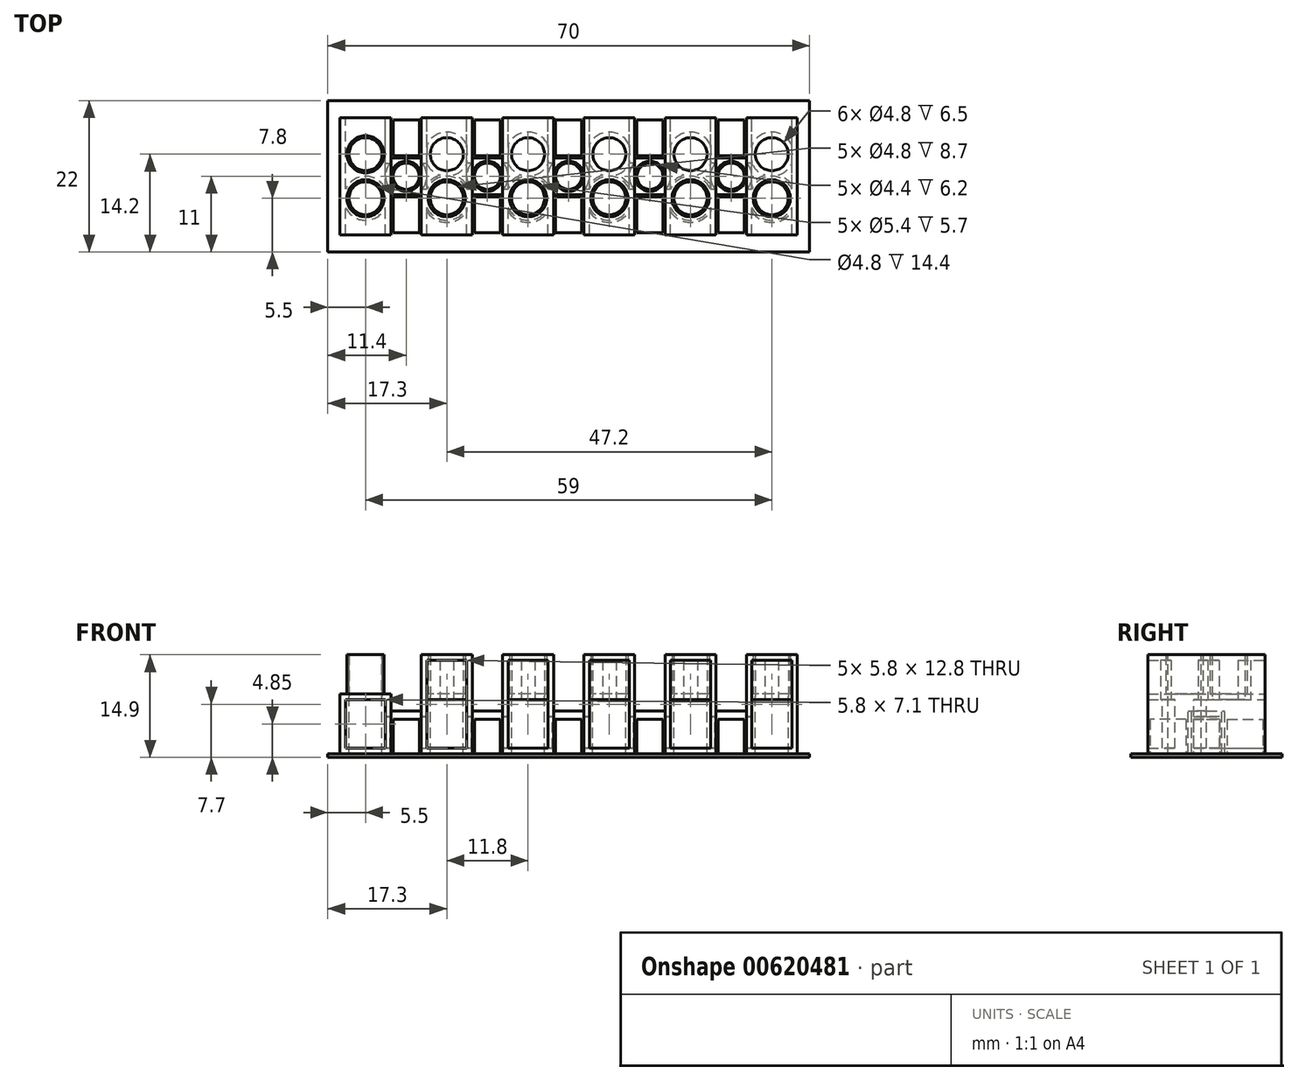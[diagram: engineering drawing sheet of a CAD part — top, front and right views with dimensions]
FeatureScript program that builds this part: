
annotation { "Feature Type Name" : "Feature", "Feature Type Description" : "" }
export const myFeature = defineFeature(function(context is Context, id is Id, definition is map)
    precondition{}
    {
        {
            var Q0;
            Q0=qCreatedBy(makeId("Top.planeOp"),FACE);
            var sketch = newSketch(context, id + "F0", { "sketchPlane" : qUnion([Q0])});
            skLineSegment(sketch, "E0.bottom", {"start": v(-25.8, -8.5) * mm, "end": v(-33.2, -8.5) * mm});
            skLineSegment(sketch, "E0.top", {"start": v(-25.8, 8.5) * mm, "end": v(-33.2, 8.5) * mm});
            skLineSegment(sketch, "E0.left", {"start": v(-25.8, -8.5) * mm, "end": v(-25.8, 8.5) * mm});
            skLineSegment(sketch, "E0.right", {"start": v(-33.2, -8.5) * mm, "end": v(-33.2, 8.5) * mm});
            skLineSegment(sketch, "E1.bottom", {"start": v(-14, -8.5) * mm, "end": v(-21.4, -8.5) * mm});
            skLineSegment(sketch, "E1.top", {"start": v(-14, 8.5) * mm, "end": v(-21.4, 8.5) * mm});
            skLineSegment(sketch, "E1.left", {"start": v(-14, -8.5) * mm, "end": v(-14, 8.5) * mm});
            skLineSegment(sketch, "E1.right", {"start": v(-21.4, -8.5) * mm, "end": v(-21.4, 8.5) * mm});
            skLineSegment(sketch, "E2.bottom", {"start": v(-2.2, -8.5) * mm, "end": v(-9.6, -8.5) * mm});
            skLineSegment(sketch, "E2.top", {"start": v(-2.2, 8.5) * mm, "end": v(-9.6, 8.5) * mm});
            skLineSegment(sketch, "E2.left", {"start": v(-2.2, -8.5) * mm, "end": v(-2.2, 8.5) * mm});
            skLineSegment(sketch, "E2.right", {"start": v(-9.6, -8.5) * mm, "end": v(-9.6, 8.5) * mm});
            skLineSegment(sketch, "E3.bottom", {"start": v(9.6, -8.5) * mm, "end": v(2.2, -8.5) * mm});
            skLineSegment(sketch, "E3.top", {"start": v(9.6, 8.5) * mm, "end": v(2.2, 8.5) * mm});
            skLineSegment(sketch, "E3.left", {"start": v(9.6, -8.5) * mm, "end": v(9.6, 8.5) * mm});
            skLineSegment(sketch, "E3.right", {"start": v(2.2, -8.5) * mm, "end": v(2.2, 8.5) * mm});
            skLineSegment(sketch, "E4.bottom", {"start": v(21.4, -8.5) * mm, "end": v(14, -8.5) * mm});
            skLineSegment(sketch, "E4.top", {"start": v(21.4, 8.5) * mm, "end": v(14, 8.5) * mm});
            skLineSegment(sketch, "E4.left", {"start": v(21.4, -8.5) * mm, "end": v(21.4, 8.5) * mm});
            skLineSegment(sketch, "E4.right", {"start": v(14, -8.5) * mm, "end": v(14, 8.5) * mm});
            skLineSegment(sketch, "E5.bottom", {"start": v(33.2, -8.5) * mm, "end": v(25.8, -8.5) * mm});
            skLineSegment(sketch, "E5.top", {"start": v(33.2, 8.5) * mm, "end": v(25.8, 8.5) * mm});
            skLineSegment(sketch, "E5.left", {"start": v(33.2, -8.5) * mm, "end": v(33.2, 8.5) * mm});
            skLineSegment(sketch, "E5.right", {"start": v(25.8, -8.5) * mm, "end": v(25.8, 8.5) * mm});
            skCircle(sketch, "E6", {"center": v(-29.5, 3.2) * mm, "radius": 2.7 * mm});
            skCircle(sketch, "E7", {"center": v(-29.5, -3.2) * mm, "radius": 2.7 * mm});
            skCircle(sketch, "E8", {"center": v(-17.7, 3.2) * mm, "radius": 2.7 * mm});
            skCircle(sketch, "E9", {"center": v(-5.9, 3.2) * mm, "radius": 2.7 * mm});
            skCircle(sketch, "E10", {"center": v(5.9, 3.2) * mm, "radius": 2.7 * mm});
            skCircle(sketch, "E11", {"center": v(17.7, 3.2) * mm, "radius": 2.7 * mm});
            skCircle(sketch, "E12", {"center": v(29.5, 3.2) * mm, "radius": 2.7 * mm});
            skCircle(sketch, "E13.MirrorC", {"center": v(-17.7, -3.2) * mm, "radius": 2.7 * mm});
            skCircle(sketch, "E14.MirrorC", {"center": v(-5.9, -3.2) * mm, "radius": 2.7 * mm});
            skCircle(sketch, "E15.MirrorC", {"center": v(5.9, -3.2) * mm, "radius": 2.7 * mm});
            skCircle(sketch, "E16.MirrorC", {"center": v(17.7, -3.2) * mm, "radius": 2.7 * mm});
            skCircle(sketch, "E17.MirrorC", {"center": v(29.5, -3.2) * mm, "radius": 2.7 * mm});
            skCircle(sketch, "E18.0", {"center": v(-29.5, 3.2) * mm, "radius": 2.4 * mm});
            skCircle(sketch, "E19.0", {"center": v(-17.7, 3.2) * mm, "radius": 2.4 * mm});
            skCircle(sketch, "E20.0", {"center": v(-5.9, 3.2) * mm, "radius": 2.4 * mm});
            skCircle(sketch, "E21.0", {"center": v(5.9, 3.2) * mm, "radius": 2.4 * mm});
            skCircle(sketch, "E22.0", {"center": v(17.7, 3.2) * mm, "radius": 2.4 * mm});
            skCircle(sketch, "E23.0", {"center": v(29.5, 3.2) * mm, "radius": 2.4 * mm});
            skCircle(sketch, "E24.MirrorC", {"center": v(-29.5, -3.2) * mm, "radius": 2.4 * mm});
            skCircle(sketch, "E25.MirrorC", {"center": v(-17.7, -3.2) * mm, "radius": 2.4 * mm});
            skCircle(sketch, "E26.MirrorC", {"center": v(-5.9, -3.2) * mm, "radius": 2.4 * mm});
            skCircle(sketch, "E27.MirrorC", {"center": v(5.9, -3.2) * mm, "radius": 2.4 * mm});
            skCircle(sketch, "E28.MirrorC", {"center": v(17.7, -3.2) * mm, "radius": 2.4 * mm});
            skCircle(sketch, "E29.MirrorC", {"center": v(29.5, -3.2) * mm, "radius": 2.4 * mm});
            skCircle(sketch, "E30", {"center": v(0, 0) * mm, "radius": 0.25 * mm, "construction": true});
            skLineSegment(sketch, "E31", {"start": v(0, 0) * mm, "end": v(0, -17.47) * mm, "construction": true});
            skLineSegment(sketch, "E32", {"start": v(-29.5, 8.5) * mm, "end": v(-29.5, -8.5) * mm, "construction": true});
            skLineSegment(sketch, "E33", {"start": v(-17.7, 8.5) * mm, "end": v(-17.7, -8.5) * mm, "construction": true});
            skLineSegment(sketch, "E34", {"start": v(-5.9, 8.5) * mm, "end": v(-5.9, -8.5) * mm, "construction": true});
            skLineSegment(sketch, "E35", {"start": v(5.9, 8.5) * mm, "end": v(5.9, -8.5) * mm, "construction": true});
            skLineSegment(sketch, "E36", {"start": v(17.7, 8.5) * mm, "end": v(17.7, -8.5) * mm, "construction": true});
            skLineSegment(sketch, "E37", {"start": v(29.5, 8.5) * mm, "end": v(29.5, -8.5) * mm, "construction": true});
            skLineSegment(sketch, "E38", {"start": v(-33.2, 0) * mm, "end": v(33.2, 0) * mm, "construction": true});
            skLineSegment(sketch, "E39", {"start": v(-25.8, 2.68) * mm, "end": v(-21.4, 2.68) * mm});
            skLineSegment(sketch, "E40", {"start": v(-25.8, -2.68) * mm, "end": v(-21.4, -2.68) * mm});
            skLineSegment(sketch, "E41", {"start": v(-14, -2.68) * mm, "end": v(-9.6, -2.68) * mm});
            skLineSegment(sketch, "E42", {"start": v(-2.2, -2.68) * mm, "end": v(2.2, -2.68) * mm});
            skLineSegment(sketch, "E43", {"start": v(9.6, -2.68) * mm, "end": v(14, -2.68) * mm});
            skLineSegment(sketch, "E44", {"start": v(21.4, -2.68) * mm, "end": v(25.8, -2.68) * mm});
            skLineSegment(sketch, "E45", {"start": v(25.8, 2.68) * mm, "end": v(21.4, 2.68) * mm});
            skLineSegment(sketch, "E46", {"start": v(14, 2.68) * mm, "end": v(9.6, 2.68) * mm});
            skLineSegment(sketch, "E47", {"start": v(2.2, 2.68) * mm, "end": v(-2.2, 2.68) * mm});
            skLineSegment(sketch, "E48", {"start": v(-9.6, 2.68) * mm, "end": v(-14, 2.68) * mm});
            skLineSegment(sketch, "E49", {"start": v(-25.8, 2.68) * mm, "end": v(-21.4, -2.68) * mm, "construction": true});
            skLineSegment(sketch, "E50", {"start": v(-14, 2.68) * mm, "end": v(-9.6, -2.68) * mm, "construction": true});
            skLineSegment(sketch, "E51", {"start": v(-2.2, 2.68) * mm, "end": v(2.2, -2.68) * mm, "construction": true});
            skLineSegment(sketch, "E52", {"start": v(9.6, 2.68) * mm, "end": v(14, -2.68) * mm, "construction": true});
            skLineSegment(sketch, "E53", {"start": v(21.4, 2.68) * mm, "end": v(25.8, -2.68) * mm, "construction": true});
            skCircle(sketch, "E54", {"center": v(-23.6, 0) * mm, "radius": 2.2 * mm});
            skCircle(sketch, "E55", {"center": v(-11.8, 0) * mm, "radius": 2.2 * mm});
            skCircle(sketch, "E56", {"center": v(0, 0) * mm, "radius": 2.2 * mm});
            skCircle(sketch, "E57", {"center": v(11.8, 0) * mm, "radius": 2.2 * mm});
            skCircle(sketch, "E58", {"center": v(23.6, 0) * mm, "radius": 2.2 * mm});
            skSolve(sketch);
        }
        {
            var Q0;
            {var subQ3=sQuery(id+"F0.wireOp",EDGE,"E0.bottom");Q0=makeQuery(id+"F0.imprint","IMPRINT",FACE,{"disambiguationData":[TD([[makeQuery(id+"F0.imprint","IMPRINT",EDGE,{"derivedFrom":subQ3}),-1.0]])]});}
            var Q1;
            {var subQ5=sQuery(id+"F0.wireOp",EDGE,"E1.bottom");Q1=makeQuery(id+"F0.imprint","IMPRINT",FACE,{"disambiguationData":[TD([[makeQuery(id+"F0.imprint","IMPRINT",EDGE,{"derivedFrom":subQ5}),-1.0]])]});}
            var Q2;
            {var subQ5=sQuery(id+"F0.wireOp",EDGE,"E2.bottom");Q2=makeQuery(id+"F0.imprint","IMPRINT",FACE,{"disambiguationData":[TD([[makeQuery(id+"F0.imprint","IMPRINT",EDGE,{"derivedFrom":subQ5}),-1.0]])]});}
            var Q3;
            {var subQ5=sQuery(id+"F0.wireOp",EDGE,"E3.bottom");Q3=makeQuery(id+"F0.imprint","IMPRINT",FACE,{"disambiguationData":[TD([[makeQuery(id+"F0.imprint","IMPRINT",EDGE,{"derivedFrom":subQ5}),-1.0]])]});}
            var Q4;
            {var subQ5=sQuery(id+"F0.wireOp",EDGE,"E4.bottom");Q4=makeQuery(id+"F0.imprint","IMPRINT",FACE,{"disambiguationData":[TD([[makeQuery(id+"F0.imprint","IMPRINT",EDGE,{"derivedFrom":subQ5}),-1.0]])]});}
            var Q5;
            {var subQ1=sQuery(id+"F0.wireOp",EDGE,"E5.bottom");Q5=makeQuery(id+"F0.imprint","IMPRINT",FACE,{"disambiguationData":[TD([[makeQuery(id+"F0.imprint","IMPRINT",EDGE,{"derivedFrom":subQ1}),-1.0]])]});}
            var Q6;
            {var subQ0=sQuery(id+"F0.wireOp",EDGE,"d3VJdfNO-Fk8P-fh5y-onYD-prEol703JRMM");Q6=makeQuery(id+"F0.imprint","IMPRINT",FACE,{"disambiguationData":[TD([[makeQuery(id+"F0.imprint","IMPRINT",EDGE,{"derivedFrom":subQ0}),1.0]])]});}
            var Q7;
            {var subQ0=sQuery(id+"F0.wireOp",EDGE,"IIVYpRpw-wNBd-OXcb-W0MZ-mRHXIPyjJA5R");Q7=makeQuery(id+"F0.imprint","IMPRINT",FACE,{"disambiguationData":[TD([[makeQuery(id+"F0.imprint","IMPRINT",EDGE,{"derivedFrom":subQ0}),1.0]])]});}
            var Q8;
            {var subQ0=sQuery(id+"F0.wireOp",EDGE,"wgGCBpVZ-QxlM-H5Bi-xMEc-6BhFhbDtORX5");Q8=makeQuery(id+"F0.imprint","IMPRINT",FACE,{"disambiguationData":[TD([[makeQuery(id+"F0.imprint","IMPRINT",EDGE,{"derivedFrom":subQ0}),-1.0]])]});}
            var Q9;
            {var subQ0=sQuery(id+"F0.wireOp",EDGE,"S4L2WrHO-g6c6-6cLC-dkaz-DY6cZUDI1iXS");Q9=makeQuery(id+"F0.imprint","IMPRINT",FACE,{"disambiguationData":[TD([[makeQuery(id+"F0.imprint","IMPRINT",EDGE,{"derivedFrom":subQ0}),-1.0]])]});}
            var Q10;
            {var subQ0=sQuery(id+"F0.wireOp",EDGE,"iaEsDPjX-zqyW-dyph-9nWc-KghkqS62flJh");Q10=makeQuery(id+"F0.imprint","IMPRINT",FACE,{"disambiguationData":[TD([[makeQuery(id+"F0.imprint","IMPRINT",EDGE,{"derivedFrom":subQ0}),-1.0]])]});}
            var Q11;
            {var subQ0=sQuery(id+"F0.wireOp",EDGE,"gJlDzY57-16t4-Vf8D-4nsT-QQv6MURsNHDC");Q11=makeQuery(id+"F0.imprint","IMPRINT",FACE,{"disambiguationData":[TD([[makeQuery(id+"F0.imprint","IMPRINT",EDGE,{"derivedFrom":subQ0}),1.0]])]});}
            var Q12;
            {var subQ0=sQuery(id+"F0.wireOp",EDGE,"vcY6GDkU-c4bm-z2yD-HaH5-KhH9jC7oKOPS");Q12=makeQuery(id+"F0.imprint","IMPRINT",FACE,{"disambiguationData":[TD([[makeQuery(id+"F0.imprint","IMPRINT",EDGE,{"derivedFrom":subQ0}),1.0]])]});}
            var Q13;
            {var subQ0=sQuery(id+"F0.wireOp",EDGE,"J0IPBTmc-wLEG-zjEr-TODg-CiZrFgkn9riR");Q13=makeQuery(id+"F0.imprint","IMPRINT",FACE,{"disambiguationData":[TD([[makeQuery(id+"F0.imprint","IMPRINT",EDGE,{"derivedFrom":subQ0}),-1.0]])]});}
            var Q14;
            {var subQ0=sQuery(id+"F0.wireOp",EDGE,"VlebEy6t-9yxg-sLxx-iXkv-Cso8guSqJYIt");Q14=makeQuery(id+"F0.imprint","IMPRINT",FACE,{"disambiguationData":[TD([[makeQuery(id+"F0.imprint","IMPRINT",EDGE,{"derivedFrom":subQ0}),-1.0]])]});}
            var Q15;
            {var subQ0=sQuery(id+"F0.wireOp",EDGE,"8PrGnW9D-uxJ0-gMwz-QmAr-Uvm73S1oeha5");Q15=makeQuery(id+"F0.imprint","IMPRINT",FACE,{"disambiguationData":[TD([[makeQuery(id+"F0.imprint","IMPRINT",EDGE,{"derivedFrom":subQ0}),1.0]])]});}
            var Q16;
            Q16=makeQuery(id+"F0.imprint","IMPRINT",FACE,{"disambiguationData":[TD([[makeQuery(id+"F0.imprint","IMPRINT",EDGE,{"derivedFrom":sQuery(id+"F0.wireOp",EDGE,"E6")}),1.0]])]});
            var Q17;
            Q17=makeQuery(id+"F0.imprint","IMPRINT",FACE,{"disambiguationData":[TD([[makeQuery(id+"F0.imprint","IMPRINT",EDGE,{"derivedFrom":sQuery(id+"F0.wireOp",EDGE,"E7")}),1.0]])]});
            var Q18;
            Q18=makeQuery(id+"F0.imprint","IMPRINT",FACE,{"disambiguationData":[TD([[makeQuery(id+"F0.imprint","IMPRINT",EDGE,{"derivedFrom":sQuery(id+"F0.wireOp",EDGE,"E13.MirrorC")}),-1.0]])]});
            var Q19;
            Q19=makeQuery(id+"F0.imprint","IMPRINT",FACE,{"disambiguationData":[TD([[makeQuery(id+"F0.imprint","IMPRINT",EDGE,{"derivedFrom":sQuery(id+"F0.wireOp",EDGE,"E8")}),1.0]])]});
            var Q20;
            Q20=makeQuery(id+"F0.imprint","IMPRINT",FACE,{"disambiguationData":[TD([[makeQuery(id+"F0.imprint","IMPRINT",EDGE,{"derivedFrom":sQuery(id+"F0.wireOp",EDGE,"E14.MirrorC")}),-1.0]])]});
            var Q21;
            Q21=makeQuery(id+"F0.imprint","IMPRINT",FACE,{"disambiguationData":[TD([[makeQuery(id+"F0.imprint","IMPRINT",EDGE,{"derivedFrom":sQuery(id+"F0.wireOp",EDGE,"E15.MirrorC")}),-1.0]])]});
            var Q22;
            Q22=makeQuery(id+"F0.imprint","IMPRINT",FACE,{"disambiguationData":[TD([[makeQuery(id+"F0.imprint","IMPRINT",EDGE,{"derivedFrom":sQuery(id+"F0.wireOp",EDGE,"E10")}),1.0]])]});
            var Q23;
            Q23=makeQuery(id+"F0.imprint","IMPRINT",FACE,{"disambiguationData":[TD([[makeQuery(id+"F0.imprint","IMPRINT",EDGE,{"derivedFrom":sQuery(id+"F0.wireOp",EDGE,"E16.MirrorC")}),-1.0]])]});
            var Q24;
            Q24=makeQuery(id+"F0.imprint","IMPRINT",FACE,{"disambiguationData":[TD([[makeQuery(id+"F0.imprint","IMPRINT",EDGE,{"derivedFrom":sQuery(id+"F0.wireOp",EDGE,"E11")}),1.0]])]});
            var Q25;
            Q25=makeQuery(id+"F0.imprint","IMPRINT",FACE,{"disambiguationData":[TD([[makeQuery(id+"F0.imprint","IMPRINT",EDGE,{"derivedFrom":sQuery(id+"F0.wireOp",EDGE,"E17.MirrorC")}),-1.0]])]});
            var Q26;
            Q26=makeQuery(id+"F0.imprint","IMPRINT",FACE,{"disambiguationData":[TD([[makeQuery(id+"F0.imprint","IMPRINT",EDGE,{"derivedFrom":sQuery(id+"F0.wireOp",EDGE,"E12")}),1.0]])]});
            var Q27;
            Q27=makeQuery(id+"F0.imprint","IMPRINT",FACE,{"disambiguationData":[TD([[makeQuery(id+"F0.imprint","IMPRINT",EDGE,{"derivedFrom":sQuery(id+"F0.wireOp",EDGE,"E9")}),1.0]])]});
            var Q28;
            Q28=makeQuery(id+"F0.imprint","IMPRINT",FACE,{"disambiguationData":[TD([[makeQuery(id+"F0.imprint","IMPRINT",EDGE,{"derivedFrom":sQuery(id+"F0.wireOp",EDGE,"E18.0")}),1.0]])]});
            var Q29;
            Q29=makeQuery(id+"F0.imprint","IMPRINT",FACE,{"disambiguationData":[TD([[makeQuery(id+"F0.imprint","IMPRINT",EDGE,{"derivedFrom":sQuery(id+"F0.wireOp",EDGE,"E24.MirrorC")}),-1.0]])]});
            var Q30;
            Q30=makeQuery(id+"F0.imprint","IMPRINT",FACE,{"disambiguationData":[TD([[makeQuery(id+"F0.imprint","IMPRINT",EDGE,{"derivedFrom":sQuery(id+"F0.wireOp",EDGE,"E19.0")}),1.0]])]});
            var Q31;
            Q31=makeQuery(id+"F0.imprint","IMPRINT",FACE,{"disambiguationData":[TD([[makeQuery(id+"F0.imprint","IMPRINT",EDGE,{"derivedFrom":sQuery(id+"F0.wireOp",EDGE,"E25.MirrorC")}),-1.0]])]});
            var Q32;
            Q32=makeQuery(id+"F0.imprint","IMPRINT",FACE,{"disambiguationData":[TD([[makeQuery(id+"F0.imprint","IMPRINT",EDGE,{"derivedFrom":sQuery(id+"F0.wireOp",EDGE,"E20.0")}),1.0]])]});
            var Q33;
            Q33=makeQuery(id+"F0.imprint","IMPRINT",FACE,{"disambiguationData":[TD([[makeQuery(id+"F0.imprint","IMPRINT",EDGE,{"derivedFrom":sQuery(id+"F0.wireOp",EDGE,"E26.MirrorC")}),-1.0]])]});
            var Q34;
            Q34=makeQuery(id+"F0.imprint","IMPRINT",FACE,{"disambiguationData":[TD([[makeQuery(id+"F0.imprint","IMPRINT",EDGE,{"derivedFrom":sQuery(id+"F0.wireOp",EDGE,"E21.0")}),1.0]])]});
            var Q35;
            Q35=makeQuery(id+"F0.imprint","IMPRINT",FACE,{"disambiguationData":[TD([[makeQuery(id+"F0.imprint","IMPRINT",EDGE,{"derivedFrom":sQuery(id+"F0.wireOp",EDGE,"E27.MirrorC")}),-1.0]])]});
            var Q36;
            Q36=makeQuery(id+"F0.imprint","IMPRINT",FACE,{"disambiguationData":[TD([[makeQuery(id+"F0.imprint","IMPRINT",EDGE,{"derivedFrom":sQuery(id+"F0.wireOp",EDGE,"E22.0")}),1.0]])]});
            var Q37;
            Q37=makeQuery(id+"F0.imprint","IMPRINT",FACE,{"disambiguationData":[TD([[makeQuery(id+"F0.imprint","IMPRINT",EDGE,{"derivedFrom":sQuery(id+"F0.wireOp",EDGE,"E28.MirrorC")}),-1.0]])]});
            var Q38;
            Q38=makeQuery(id+"F0.imprint","IMPRINT",FACE,{"disambiguationData":[TD([[makeQuery(id+"F0.imprint","IMPRINT",EDGE,{"derivedFrom":sQuery(id+"F0.wireOp",EDGE,"E29.MirrorC")}),-1.0]])]});
            var Q39;
            Q39=makeQuery(id+"F0.imprint","IMPRINT",FACE,{"disambiguationData":[TD([[makeQuery(id+"F0.imprint","IMPRINT",EDGE,{"derivedFrom":sQuery(id+"F0.wireOp",EDGE,"E23.0")}),1.0]])]});
            var Q40;
            {var subQ0=sQuery(id+"F0.wireOp",EDGE,"E40");Q40=makeQuery(id+"F0.imprint","IMPRINT",FACE,{"disambiguationData":[TD([[makeQuery(id+"F0.imprint","IMPRINT",EDGE,{"derivedFrom":subQ0}),1.0]])]});}
            var Q41;
            {var subQ0=sQuery(id+"F0.wireOp",EDGE,"E39");Q41=makeQuery(id+"F0.imprint","IMPRINT",FACE,{"disambiguationData":[TD([[makeQuery(id+"F0.imprint","IMPRINT",EDGE,{"derivedFrom":subQ0}),-1.0]])]});}
            var Q42;
            {var subQ0=sQuery(id+"F0.wireOp",EDGE,"E48");Q42=makeQuery(id+"F0.imprint","IMPRINT",FACE,{"disambiguationData":[TD([[makeQuery(id+"F0.imprint","IMPRINT",EDGE,{"derivedFrom":subQ0}),1.0]])]});}
            var Q43;
            {var subQ0=sQuery(id+"F0.wireOp",EDGE,"E41");Q43=makeQuery(id+"F0.imprint","IMPRINT",FACE,{"disambiguationData":[TD([[makeQuery(id+"F0.imprint","IMPRINT",EDGE,{"derivedFrom":subQ0}),1.0]])]});}
            var Q44;
            {var subQ0=sQuery(id+"F0.wireOp",EDGE,"E47");Q44=makeQuery(id+"F0.imprint","IMPRINT",FACE,{"disambiguationData":[TD([[makeQuery(id+"F0.imprint","IMPRINT",EDGE,{"derivedFrom":subQ0}),1.0]])]});}
            var Q45;
            {var subQ0=sQuery(id+"F0.wireOp",EDGE,"E42");Q45=makeQuery(id+"F0.imprint","IMPRINT",FACE,{"disambiguationData":[TD([[makeQuery(id+"F0.imprint","IMPRINT",EDGE,{"derivedFrom":subQ0}),1.0]])]});}
            var Q46;
            {var subQ0=sQuery(id+"F0.wireOp",EDGE,"E46");Q46=makeQuery(id+"F0.imprint","IMPRINT",FACE,{"disambiguationData":[TD([[makeQuery(id+"F0.imprint","IMPRINT",EDGE,{"derivedFrom":subQ0}),1.0]])]});}
            var Q47;
            {var subQ0=sQuery(id+"F0.wireOp",EDGE,"E43");Q47=makeQuery(id+"F0.imprint","IMPRINT",FACE,{"disambiguationData":[TD([[makeQuery(id+"F0.imprint","IMPRINT",EDGE,{"derivedFrom":subQ0}),1.0]])]});}
            var Q48;
            {var subQ0=sQuery(id+"F0.wireOp",EDGE,"E45");Q48=makeQuery(id+"F0.imprint","IMPRINT",FACE,{"disambiguationData":[TD([[makeQuery(id+"F0.imprint","IMPRINT",EDGE,{"derivedFrom":subQ0}),1.0]])]});}
            var Q49;
            {var subQ0=sQuery(id+"F0.wireOp",EDGE,"E44");Q49=makeQuery(id+"F0.imprint","IMPRINT",FACE,{"disambiguationData":[TD([[makeQuery(id+"F0.imprint","IMPRINT",EDGE,{"derivedFrom":subQ0}),1.0]])]});}
            extrude(context, id + "F1", {"entities" : qUnion([Q0, Q1, Q2, Q3, Q4, Q5, Q6, Q7, Q8, Q9, Q10, Q11, Q12, Q13, Q14, Q15, Q16, Q17, Q18, Q19, Q20, Q21, Q22, Q23, Q24, Q25, Q26, Q27, Q28, Q29, Q30, Q31, Q32, Q33, Q34, Q35, Q36, Q37, Q38, Q39, Q40, Q41, Q42, Q43, Q44, Q45, Q46, Q47, Q48, Q49]), "oppositeDirection" : true, "depth" : 8.7 * mm, "offsetDistance" : 25 * mm});
        }
        {
            var Q0;
            Q0=makeQuery(id+"F0.imprint","IMPRINT",FACE,{"disambiguationData":[TD([[makeQuery(id+"F0.imprint","IMPRINT",EDGE,{"derivedFrom":sQuery(id+"F0.wireOp",EDGE,"E7")}),1.0]])]});
            var Q1;
            Q1=makeQuery(id+"F0.imprint","IMPRINT",FACE,{"disambiguationData":[TD([[makeQuery(id+"F0.imprint","IMPRINT",EDGE,{"derivedFrom":sQuery(id+"F0.wireOp",EDGE,"E6")}),1.0]])]});
            var Q2;
            Q2=makeQuery(id+"F0.imprint","IMPRINT",FACE,{"disambiguationData":[TD([[makeQuery(id+"F0.imprint","IMPRINT",EDGE,{"derivedFrom":sQuery(id+"F0.wireOp",EDGE,"E8")}),1.0]])]});
            var Q3;
            Q3=makeQuery(id+"F0.imprint","IMPRINT",FACE,{"disambiguationData":[TD([[makeQuery(id+"F0.imprint","IMPRINT",EDGE,{"derivedFrom":sQuery(id+"F0.wireOp",EDGE,"E13.MirrorC")}),-1.0]])]});
            var Q4;
            Q4=makeQuery(id+"F0.imprint","IMPRINT",FACE,{"disambiguationData":[TD([[makeQuery(id+"F0.imprint","IMPRINT",EDGE,{"derivedFrom":sQuery(id+"F0.wireOp",EDGE,"E14.MirrorC")}),-1.0]])]});
            var Q5;
            Q5=makeQuery(id+"F0.imprint","IMPRINT",FACE,{"disambiguationData":[TD([[makeQuery(id+"F0.imprint","IMPRINT",EDGE,{"derivedFrom":sQuery(id+"F0.wireOp",EDGE,"E9")}),1.0]])]});
            var Q6;
            Q6=makeQuery(id+"F0.imprint","IMPRINT",FACE,{"disambiguationData":[TD([[makeQuery(id+"F0.imprint","IMPRINT",EDGE,{"derivedFrom":sQuery(id+"F0.wireOp",EDGE,"E15.MirrorC")}),-1.0]])]});
            var Q7;
            Q7=makeQuery(id+"F0.imprint","IMPRINT",FACE,{"disambiguationData":[TD([[makeQuery(id+"F0.imprint","IMPRINT",EDGE,{"derivedFrom":sQuery(id+"F0.wireOp",EDGE,"E10")}),1.0]])]});
            var Q8;
            Q8=makeQuery(id+"F0.imprint","IMPRINT",FACE,{"disambiguationData":[TD([[makeQuery(id+"F0.imprint","IMPRINT",EDGE,{"derivedFrom":sQuery(id+"F0.wireOp",EDGE,"E11")}),1.0]])]});
            var Q9;
            Q9=makeQuery(id+"F0.imprint","IMPRINT",FACE,{"disambiguationData":[TD([[makeQuery(id+"F0.imprint","IMPRINT",EDGE,{"derivedFrom":sQuery(id+"F0.wireOp",EDGE,"E16.MirrorC")}),-1.0]])]});
            var Q10;
            Q10=makeQuery(id+"F0.imprint","IMPRINT",FACE,{"disambiguationData":[TD([[makeQuery(id+"F0.imprint","IMPRINT",EDGE,{"derivedFrom":sQuery(id+"F0.wireOp",EDGE,"E12")}),1.0]])]});
            var Q11;
            Q11=makeQuery(id+"F0.imprint","IMPRINT",FACE,{"disambiguationData":[TD([[makeQuery(id+"F0.imprint","IMPRINT",EDGE,{"derivedFrom":sQuery(id+"F0.wireOp",EDGE,"E17.MirrorC")}),-1.0]])]});
            extrude(context, id + "F2", {"entities" : qUnion([Q0, Q1, Q2, Q3, Q4, Q5, Q6, Q7, Q8, Q9, Q10, Q11]), "operationType" : NewBodyOperationType.ADD, "depth" : 5.7 * mm, "offsetDistance" : 25 * mm});
        }
        {
            var Q0;
            {var subQ0=sQuery(id+"F0.wireOp",EDGE,"E39");Q0=makeQuery(id+"F0.imprint","IMPRINT",FACE,{"disambiguationData":[TD([[makeQuery(id+"F0.imprint","IMPRINT",EDGE,{"derivedFrom":subQ0}),-1.0]])]});}
            var Q1;
            {var subQ0=sQuery(id+"F0.wireOp",EDGE,"E40");Q1=makeQuery(id+"F0.imprint","IMPRINT",FACE,{"disambiguationData":[TD([[makeQuery(id+"F0.imprint","IMPRINT",EDGE,{"derivedFrom":subQ0}),1.0]])]});}
            var Q2;
            {var subQ0=sQuery(id+"F0.wireOp",EDGE,"E48");Q2=makeQuery(id+"F0.imprint","IMPRINT",FACE,{"disambiguationData":[TD([[makeQuery(id+"F0.imprint","IMPRINT",EDGE,{"derivedFrom":subQ0}),1.0]])]});}
            var Q3;
            {var subQ0=sQuery(id+"F0.wireOp",EDGE,"E41");Q3=makeQuery(id+"F0.imprint","IMPRINT",FACE,{"disambiguationData":[TD([[makeQuery(id+"F0.imprint","IMPRINT",EDGE,{"derivedFrom":subQ0}),1.0]])]});}
            var Q4;
            {var subQ0=sQuery(id+"F0.wireOp",EDGE,"E47");Q4=makeQuery(id+"F0.imprint","IMPRINT",FACE,{"disambiguationData":[TD([[makeQuery(id+"F0.imprint","IMPRINT",EDGE,{"derivedFrom":subQ0}),1.0]])]});}
            var Q5;
            {var subQ0=sQuery(id+"F0.wireOp",EDGE,"E42");Q5=makeQuery(id+"F0.imprint","IMPRINT",FACE,{"disambiguationData":[TD([[makeQuery(id+"F0.imprint","IMPRINT",EDGE,{"derivedFrom":subQ0}),1.0]])]});}
            var Q6;
            {var subQ0=sQuery(id+"F0.wireOp",EDGE,"E46");Q6=makeQuery(id+"F0.imprint","IMPRINT",FACE,{"disambiguationData":[TD([[makeQuery(id+"F0.imprint","IMPRINT",EDGE,{"derivedFrom":subQ0}),1.0]])]});}
            var Q7;
            {var subQ0=sQuery(id+"F0.wireOp",EDGE,"E43");Q7=makeQuery(id+"F0.imprint","IMPRINT",FACE,{"disambiguationData":[TD([[makeQuery(id+"F0.imprint","IMPRINT",EDGE,{"derivedFrom":subQ0}),1.0]])]});}
            var Q8;
            {var subQ0=sQuery(id+"F0.wireOp",EDGE,"E45");Q8=makeQuery(id+"F0.imprint","IMPRINT",FACE,{"disambiguationData":[TD([[makeQuery(id+"F0.imprint","IMPRINT",EDGE,{"derivedFrom":subQ0}),1.0]])]});}
            var Q9;
            {var subQ0=sQuery(id+"F0.wireOp",EDGE,"E44");Q9=makeQuery(id+"F0.imprint","IMPRINT",FACE,{"disambiguationData":[TD([[makeQuery(id+"F0.imprint","IMPRINT",EDGE,{"derivedFrom":subQ0}),1.0]])]});}
            extrude(context, id + "F3", {"entities" : qUnion([Q0, Q1, Q2, Q3, Q4, Q5, Q6, Q7, Q8, Q9]), "operationType" : NewBodyOperationType.REMOVE, "oppositeDirection" : true, "depth" : 2.5 * mm, "offsetDistance" : 25 * mm});
        }
        {
            var Q0;
            Q0=makeQuery(id+"F1.opExtrude","SWEPT_FACE",FACE,{"disambiguationData":[OSD([sQuery(id+"F0.wireOp",EDGE,"E5.top")])]});
            var Q1;
            Q1=makeQuery(id+"F1.opExtrude","SWEPT_FACE",FACE,{"disambiguationData":[OSD([sQuery(id+"F0.wireOp",EDGE,"E5.bottom")])]});
            var Q2;
            Q2=makeQuery(id+"F1.opExtrude","SWEPT_FACE",FACE,{"disambiguationData":[OSD([sQuery(id+"F0.wireOp",EDGE,"E4.bottom")])]});
            var Q3;
            Q3=makeQuery(id+"F1.opExtrude","SWEPT_FACE",FACE,{"disambiguationData":[OSD([sQuery(id+"F0.wireOp",EDGE,"E4.top")])]});
            var Q4;
            Q4=makeQuery(id+"F1.opExtrude","SWEPT_FACE",FACE,{"disambiguationData":[OSD([sQuery(id+"F0.wireOp",EDGE,"E3.bottom")])]});
            var Q5;
            Q5=makeQuery(id+"F1.opExtrude","SWEPT_FACE",FACE,{"disambiguationData":[OSD([sQuery(id+"F0.wireOp",EDGE,"E3.top")])]});
            var Q6;
            Q6=makeQuery(id+"F1.opExtrude","SWEPT_FACE",FACE,{"disambiguationData":[OSD([sQuery(id+"F0.wireOp",EDGE,"E2.bottom")])]});
            var Q7;
            Q7=makeQuery(id+"F1.opExtrude","SWEPT_FACE",FACE,{"disambiguationData":[OSD([sQuery(id+"F0.wireOp",EDGE,"E2.top")])]});
            var Q8;
            Q8=makeQuery(id+"F1.opExtrude","SWEPT_FACE",FACE,{"disambiguationData":[OSD([sQuery(id+"F0.wireOp",EDGE,"E1.bottom")])]});
            var Q9;
            Q9=makeQuery(id+"F1.opExtrude","SWEPT_FACE",FACE,{"disambiguationData":[OSD([sQuery(id+"F0.wireOp",EDGE,"E1.top")])]});
            var Q10;
            Q10=makeQuery(id+"F1.opExtrude","SWEPT_FACE",FACE,{"disambiguationData":[OSD([sQuery(id+"F0.wireOp",EDGE,"E0.bottom")])]});
            var Q11;
            Q11=makeQuery(id+"F1.opExtrude","SWEPT_FACE",FACE,{"disambiguationData":[OSD([sQuery(id+"F0.wireOp",EDGE,"E0.top")])]});
            shell(context, id + "F4", {"entities" : qUnion([Q0, Q1, Q2, Q3, Q4, Q5, Q6, Q7, Q8, Q9, Q10, Q11]), "thickness" : 0.8 * mm});
        }
        {
            var Q0;
            Q0=makeQuery(id+"F2.boolean.opBoolean","SPLIT",FACE,{"disambiguationData":[TD([makeQuery(id+"F2.opExtrude","SWEPT_FACE",FACE,{"disambiguationData":[OSD([sQuery(id+"F0.wireOp",EDGE,"E29.MirrorC")])]})])],"derivedFrom":makeQuery(id+"F1.opExtrude","CAP_FACE",FACE,{"disambiguationData":[OSD([sQuery(id+"F0.wireOp",EDGE,"E0.bottom"),sQuery(id+"F0.wireOp",EDGE,"E0.top"),sQuery(id+"F0.wireOp",EDGE,"E0.left"),sQuery(id+"F0.wireOp",EDGE,"E0.right"),sQuery(id+"F0.wireOp",EDGE,"E1.bottom"),sQuery(id+"F0.wireOp",EDGE,"E1.top"),sQuery(id+"F0.wireOp",EDGE,"E1.left"),sQuery(id+"F0.wireOp",EDGE,"E1.right"),sQuery(id+"F0.wireOp",EDGE,"E2.bottom"),sQuery(id+"F0.wireOp",EDGE,"E2.top"),sQuery(id+"F0.wireOp",EDGE,"E2.left"),sQuery(id+"F0.wireOp",EDGE,"E2.right"),sQuery(id+"F0.wireOp",EDGE,"E3.bottom"),sQuery(id+"F0.wireOp",EDGE,"E3.top"),sQuery(id+"F0.wireOp",EDGE,"E3.left"),sQuery(id+"F0.wireOp",EDGE,"E3.right"),sQuery(id+"F0.wireOp",EDGE,"E4.bottom"),sQuery(id+"F0.wireOp",EDGE,"E4.top"),sQuery(id+"F0.wireOp",EDGE,"E4.left"),sQuery(id+"F0.wireOp",EDGE,"E4.right"),sQuery(id+"F0.wireOp",EDGE,"E5.bottom"),sQuery(id+"F0.wireOp",EDGE,"E5.top"),sQuery(id+"F0.wireOp",EDGE,"E5.left"),sQuery(id+"F0.wireOp",EDGE,"E5.right"),sQuery(id+"F0.wireOp",EDGE,"cyoVeOsO-Ylvr-umjH-xySE-kTFhUaTDjDfD"),sQuery(id+"F0.wireOp",EDGE,"3eRy93ct-3uHp-ltHB-iF47-y57oyBoY3byI"),sQuery(id+"F0.wireOp",EDGE,"lrmn35il-Zq5m-sfIJ-5385-KA4XqFf2W20m"),sQuery(id+"F0.wireOp",EDGE,"QQd6hot7-zCFL-FVzE-QJR4-5pPOlfIRa5t9"),sQuery(id+"F0.wireOp",EDGE,"atnKaNye-AkJt-ZNtv-891p-w1etO83M4aAZ"),sQuery(id+"F0.wireOp",EDGE,"VlebEy6t-9yxg-sLxx-iXkv-Cso8guSqJYIt"),sQuery(id+"F0.wireOp",EDGE,"8PrGnW9D-uxJ0-gMwz-QmAr-Uvm73S1oeha5"),sQuery(id+"F0.wireOp",EDGE,"J0IPBTmc-wLEG-zjEr-TODg-CiZrFgkn9riR"),sQuery(id+"F0.wireOp",EDGE,"vcY6GDkU-c4bm-z2yD-HaH5-KhH9jC7oKOPS"),sQuery(id+"F0.wireOp",EDGE,"iaEsDPjX-zqyW-dyph-9nWc-KghkqS62flJh"),sQuery(id+"F0.wireOp",EDGE,"gJlDzY57-16t4-Vf8D-4nsT-QQv6MURsNHDC"),sQuery(id+"F0.wireOp",EDGE,"S4L2WrHO-g6c6-6cLC-dkaz-DY6cZUDI1iXS"),sQuery(id+"F0.wireOp",EDGE,"IIVYpRpw-wNBd-OXcb-W0MZ-mRHXIPyjJA5R"),sQuery(id+"F0.wireOp",EDGE,"wgGCBpVZ-QxlM-H5Bi-xMEc-6BhFhbDtORX5"),sQuery(id+"F0.wireOp",EDGE,"d3VJdfNO-Fk8P-fh5y-onYD-prEol703JRMM")])],"isStart":true})});
            var Q1;
            Q1=makeQuery(id+"F2.boolean.opBoolean","SPLIT",FACE,{"disambiguationData":[TD([makeQuery(id+"F2.opExtrude","SWEPT_FACE",FACE,{"disambiguationData":[OSD([sQuery(id+"F0.wireOp",EDGE,"E23.0")])]})])],"derivedFrom":makeQuery(id+"F1.opExtrude","CAP_FACE",FACE,{"disambiguationData":[OSD([sQuery(id+"F0.wireOp",EDGE,"E0.bottom"),sQuery(id+"F0.wireOp",EDGE,"E0.top"),sQuery(id+"F0.wireOp",EDGE,"E0.left"),sQuery(id+"F0.wireOp",EDGE,"E0.right"),sQuery(id+"F0.wireOp",EDGE,"E1.bottom"),sQuery(id+"F0.wireOp",EDGE,"E1.top"),sQuery(id+"F0.wireOp",EDGE,"E1.left"),sQuery(id+"F0.wireOp",EDGE,"E1.right"),sQuery(id+"F0.wireOp",EDGE,"E2.bottom"),sQuery(id+"F0.wireOp",EDGE,"E2.top"),sQuery(id+"F0.wireOp",EDGE,"E2.left"),sQuery(id+"F0.wireOp",EDGE,"E2.right"),sQuery(id+"F0.wireOp",EDGE,"E3.bottom"),sQuery(id+"F0.wireOp",EDGE,"E3.top"),sQuery(id+"F0.wireOp",EDGE,"E3.left"),sQuery(id+"F0.wireOp",EDGE,"E3.right"),sQuery(id+"F0.wireOp",EDGE,"E4.bottom"),sQuery(id+"F0.wireOp",EDGE,"E4.top"),sQuery(id+"F0.wireOp",EDGE,"E4.left"),sQuery(id+"F0.wireOp",EDGE,"E4.right"),sQuery(id+"F0.wireOp",EDGE,"E5.bottom"),sQuery(id+"F0.wireOp",EDGE,"E5.top"),sQuery(id+"F0.wireOp",EDGE,"E5.left"),sQuery(id+"F0.wireOp",EDGE,"E5.right"),sQuery(id+"F0.wireOp",EDGE,"cyoVeOsO-Ylvr-umjH-xySE-kTFhUaTDjDfD"),sQuery(id+"F0.wireOp",EDGE,"3eRy93ct-3uHp-ltHB-iF47-y57oyBoY3byI"),sQuery(id+"F0.wireOp",EDGE,"lrmn35il-Zq5m-sfIJ-5385-KA4XqFf2W20m"),sQuery(id+"F0.wireOp",EDGE,"QQd6hot7-zCFL-FVzE-QJR4-5pPOlfIRa5t9"),sQuery(id+"F0.wireOp",EDGE,"atnKaNye-AkJt-ZNtv-891p-w1etO83M4aAZ"),sQuery(id+"F0.wireOp",EDGE,"VlebEy6t-9yxg-sLxx-iXkv-Cso8guSqJYIt"),sQuery(id+"F0.wireOp",EDGE,"8PrGnW9D-uxJ0-gMwz-QmAr-Uvm73S1oeha5"),sQuery(id+"F0.wireOp",EDGE,"J0IPBTmc-wLEG-zjEr-TODg-CiZrFgkn9riR"),sQuery(id+"F0.wireOp",EDGE,"vcY6GDkU-c4bm-z2yD-HaH5-KhH9jC7oKOPS"),sQuery(id+"F0.wireOp",EDGE,"iaEsDPjX-zqyW-dyph-9nWc-KghkqS62flJh"),sQuery(id+"F0.wireOp",EDGE,"gJlDzY57-16t4-Vf8D-4nsT-QQv6MURsNHDC"),sQuery(id+"F0.wireOp",EDGE,"S4L2WrHO-g6c6-6cLC-dkaz-DY6cZUDI1iXS"),sQuery(id+"F0.wireOp",EDGE,"IIVYpRpw-wNBd-OXcb-W0MZ-mRHXIPyjJA5R"),sQuery(id+"F0.wireOp",EDGE,"wgGCBpVZ-QxlM-H5Bi-xMEc-6BhFhbDtORX5"),sQuery(id+"F0.wireOp",EDGE,"d3VJdfNO-Fk8P-fh5y-onYD-prEol703JRMM")])],"isStart":true})});
            var Q2;
            Q2=makeQuery(id+"F2.boolean.opBoolean","SPLIT",FACE,{"disambiguationData":[TD([makeQuery(id+"F2.opExtrude","SWEPT_FACE",FACE,{"disambiguationData":[OSD([sQuery(id+"F0.wireOp",EDGE,"E22.0")])]})])],"derivedFrom":makeQuery(id+"F1.opExtrude","CAP_FACE",FACE,{"disambiguationData":[OSD([sQuery(id+"F0.wireOp",EDGE,"E0.bottom"),sQuery(id+"F0.wireOp",EDGE,"E0.top"),sQuery(id+"F0.wireOp",EDGE,"E0.left"),sQuery(id+"F0.wireOp",EDGE,"E0.right"),sQuery(id+"F0.wireOp",EDGE,"E1.bottom"),sQuery(id+"F0.wireOp",EDGE,"E1.top"),sQuery(id+"F0.wireOp",EDGE,"E1.left"),sQuery(id+"F0.wireOp",EDGE,"E1.right"),sQuery(id+"F0.wireOp",EDGE,"E2.bottom"),sQuery(id+"F0.wireOp",EDGE,"E2.top"),sQuery(id+"F0.wireOp",EDGE,"E2.left"),sQuery(id+"F0.wireOp",EDGE,"E2.right"),sQuery(id+"F0.wireOp",EDGE,"E3.bottom"),sQuery(id+"F0.wireOp",EDGE,"E3.top"),sQuery(id+"F0.wireOp",EDGE,"E3.left"),sQuery(id+"F0.wireOp",EDGE,"E3.right"),sQuery(id+"F0.wireOp",EDGE,"E4.bottom"),sQuery(id+"F0.wireOp",EDGE,"E4.top"),sQuery(id+"F0.wireOp",EDGE,"E4.left"),sQuery(id+"F0.wireOp",EDGE,"E4.right"),sQuery(id+"F0.wireOp",EDGE,"E5.bottom"),sQuery(id+"F0.wireOp",EDGE,"E5.top"),sQuery(id+"F0.wireOp",EDGE,"E5.left"),sQuery(id+"F0.wireOp",EDGE,"E5.right"),sQuery(id+"F0.wireOp",EDGE,"cyoVeOsO-Ylvr-umjH-xySE-kTFhUaTDjDfD"),sQuery(id+"F0.wireOp",EDGE,"3eRy93ct-3uHp-ltHB-iF47-y57oyBoY3byI"),sQuery(id+"F0.wireOp",EDGE,"lrmn35il-Zq5m-sfIJ-5385-KA4XqFf2W20m"),sQuery(id+"F0.wireOp",EDGE,"QQd6hot7-zCFL-FVzE-QJR4-5pPOlfIRa5t9"),sQuery(id+"F0.wireOp",EDGE,"atnKaNye-AkJt-ZNtv-891p-w1etO83M4aAZ"),sQuery(id+"F0.wireOp",EDGE,"VlebEy6t-9yxg-sLxx-iXkv-Cso8guSqJYIt"),sQuery(id+"F0.wireOp",EDGE,"8PrGnW9D-uxJ0-gMwz-QmAr-Uvm73S1oeha5"),sQuery(id+"F0.wireOp",EDGE,"J0IPBTmc-wLEG-zjEr-TODg-CiZrFgkn9riR"),sQuery(id+"F0.wireOp",EDGE,"vcY6GDkU-c4bm-z2yD-HaH5-KhH9jC7oKOPS"),sQuery(id+"F0.wireOp",EDGE,"iaEsDPjX-zqyW-dyph-9nWc-KghkqS62flJh"),sQuery(id+"F0.wireOp",EDGE,"gJlDzY57-16t4-Vf8D-4nsT-QQv6MURsNHDC"),sQuery(id+"F0.wireOp",EDGE,"S4L2WrHO-g6c6-6cLC-dkaz-DY6cZUDI1iXS"),sQuery(id+"F0.wireOp",EDGE,"IIVYpRpw-wNBd-OXcb-W0MZ-mRHXIPyjJA5R"),sQuery(id+"F0.wireOp",EDGE,"wgGCBpVZ-QxlM-H5Bi-xMEc-6BhFhbDtORX5"),sQuery(id+"F0.wireOp",EDGE,"d3VJdfNO-Fk8P-fh5y-onYD-prEol703JRMM")])],"isStart":true})});
            var Q3;
            Q3=makeQuery(id+"F2.boolean.opBoolean","SPLIT",FACE,{"disambiguationData":[TD([makeQuery(id+"F2.opExtrude","SWEPT_FACE",FACE,{"disambiguationData":[OSD([sQuery(id+"F0.wireOp",EDGE,"E28.MirrorC")])]})])],"derivedFrom":makeQuery(id+"F1.opExtrude","CAP_FACE",FACE,{"disambiguationData":[OSD([sQuery(id+"F0.wireOp",EDGE,"E0.bottom"),sQuery(id+"F0.wireOp",EDGE,"E0.top"),sQuery(id+"F0.wireOp",EDGE,"E0.left"),sQuery(id+"F0.wireOp",EDGE,"E0.right"),sQuery(id+"F0.wireOp",EDGE,"E1.bottom"),sQuery(id+"F0.wireOp",EDGE,"E1.top"),sQuery(id+"F0.wireOp",EDGE,"E1.left"),sQuery(id+"F0.wireOp",EDGE,"E1.right"),sQuery(id+"F0.wireOp",EDGE,"E2.bottom"),sQuery(id+"F0.wireOp",EDGE,"E2.top"),sQuery(id+"F0.wireOp",EDGE,"E2.left"),sQuery(id+"F0.wireOp",EDGE,"E2.right"),sQuery(id+"F0.wireOp",EDGE,"E3.bottom"),sQuery(id+"F0.wireOp",EDGE,"E3.top"),sQuery(id+"F0.wireOp",EDGE,"E3.left"),sQuery(id+"F0.wireOp",EDGE,"E3.right"),sQuery(id+"F0.wireOp",EDGE,"E4.bottom"),sQuery(id+"F0.wireOp",EDGE,"E4.top"),sQuery(id+"F0.wireOp",EDGE,"E4.left"),sQuery(id+"F0.wireOp",EDGE,"E4.right"),sQuery(id+"F0.wireOp",EDGE,"E5.bottom"),sQuery(id+"F0.wireOp",EDGE,"E5.top"),sQuery(id+"F0.wireOp",EDGE,"E5.left"),sQuery(id+"F0.wireOp",EDGE,"E5.right"),sQuery(id+"F0.wireOp",EDGE,"cyoVeOsO-Ylvr-umjH-xySE-kTFhUaTDjDfD"),sQuery(id+"F0.wireOp",EDGE,"3eRy93ct-3uHp-ltHB-iF47-y57oyBoY3byI"),sQuery(id+"F0.wireOp",EDGE,"lrmn35il-Zq5m-sfIJ-5385-KA4XqFf2W20m"),sQuery(id+"F0.wireOp",EDGE,"QQd6hot7-zCFL-FVzE-QJR4-5pPOlfIRa5t9"),sQuery(id+"F0.wireOp",EDGE,"atnKaNye-AkJt-ZNtv-891p-w1etO83M4aAZ"),sQuery(id+"F0.wireOp",EDGE,"VlebEy6t-9yxg-sLxx-iXkv-Cso8guSqJYIt"),sQuery(id+"F0.wireOp",EDGE,"8PrGnW9D-uxJ0-gMwz-QmAr-Uvm73S1oeha5"),sQuery(id+"F0.wireOp",EDGE,"J0IPBTmc-wLEG-zjEr-TODg-CiZrFgkn9riR"),sQuery(id+"F0.wireOp",EDGE,"vcY6GDkU-c4bm-z2yD-HaH5-KhH9jC7oKOPS"),sQuery(id+"F0.wireOp",EDGE,"iaEsDPjX-zqyW-dyph-9nWc-KghkqS62flJh"),sQuery(id+"F0.wireOp",EDGE,"gJlDzY57-16t4-Vf8D-4nsT-QQv6MURsNHDC"),sQuery(id+"F0.wireOp",EDGE,"S4L2WrHO-g6c6-6cLC-dkaz-DY6cZUDI1iXS"),sQuery(id+"F0.wireOp",EDGE,"IIVYpRpw-wNBd-OXcb-W0MZ-mRHXIPyjJA5R"),sQuery(id+"F0.wireOp",EDGE,"wgGCBpVZ-QxlM-H5Bi-xMEc-6BhFhbDtORX5"),sQuery(id+"F0.wireOp",EDGE,"d3VJdfNO-Fk8P-fh5y-onYD-prEol703JRMM")])],"isStart":true})});
            var Q4;
            Q4=makeQuery(id+"F2.boolean.opBoolean","SPLIT",FACE,{"disambiguationData":[TD([makeQuery(id+"F2.opExtrude","SWEPT_FACE",FACE,{"disambiguationData":[OSD([sQuery(id+"F0.wireOp",EDGE,"E27.MirrorC")])]})])],"derivedFrom":makeQuery(id+"F1.opExtrude","CAP_FACE",FACE,{"disambiguationData":[OSD([sQuery(id+"F0.wireOp",EDGE,"E0.bottom"),sQuery(id+"F0.wireOp",EDGE,"E0.top"),sQuery(id+"F0.wireOp",EDGE,"E0.left"),sQuery(id+"F0.wireOp",EDGE,"E0.right"),sQuery(id+"F0.wireOp",EDGE,"E1.bottom"),sQuery(id+"F0.wireOp",EDGE,"E1.top"),sQuery(id+"F0.wireOp",EDGE,"E1.left"),sQuery(id+"F0.wireOp",EDGE,"E1.right"),sQuery(id+"F0.wireOp",EDGE,"E2.bottom"),sQuery(id+"F0.wireOp",EDGE,"E2.top"),sQuery(id+"F0.wireOp",EDGE,"E2.left"),sQuery(id+"F0.wireOp",EDGE,"E2.right"),sQuery(id+"F0.wireOp",EDGE,"E3.bottom"),sQuery(id+"F0.wireOp",EDGE,"E3.top"),sQuery(id+"F0.wireOp",EDGE,"E3.left"),sQuery(id+"F0.wireOp",EDGE,"E3.right"),sQuery(id+"F0.wireOp",EDGE,"E4.bottom"),sQuery(id+"F0.wireOp",EDGE,"E4.top"),sQuery(id+"F0.wireOp",EDGE,"E4.left"),sQuery(id+"F0.wireOp",EDGE,"E4.right"),sQuery(id+"F0.wireOp",EDGE,"E5.bottom"),sQuery(id+"F0.wireOp",EDGE,"E5.top"),sQuery(id+"F0.wireOp",EDGE,"E5.left"),sQuery(id+"F0.wireOp",EDGE,"E5.right"),sQuery(id+"F0.wireOp",EDGE,"cyoVeOsO-Ylvr-umjH-xySE-kTFhUaTDjDfD"),sQuery(id+"F0.wireOp",EDGE,"3eRy93ct-3uHp-ltHB-iF47-y57oyBoY3byI"),sQuery(id+"F0.wireOp",EDGE,"lrmn35il-Zq5m-sfIJ-5385-KA4XqFf2W20m"),sQuery(id+"F0.wireOp",EDGE,"QQd6hot7-zCFL-FVzE-QJR4-5pPOlfIRa5t9"),sQuery(id+"F0.wireOp",EDGE,"atnKaNye-AkJt-ZNtv-891p-w1etO83M4aAZ"),sQuery(id+"F0.wireOp",EDGE,"VlebEy6t-9yxg-sLxx-iXkv-Cso8guSqJYIt"),sQuery(id+"F0.wireOp",EDGE,"8PrGnW9D-uxJ0-gMwz-QmAr-Uvm73S1oeha5"),sQuery(id+"F0.wireOp",EDGE,"J0IPBTmc-wLEG-zjEr-TODg-CiZrFgkn9riR"),sQuery(id+"F0.wireOp",EDGE,"vcY6GDkU-c4bm-z2yD-HaH5-KhH9jC7oKOPS"),sQuery(id+"F0.wireOp",EDGE,"iaEsDPjX-zqyW-dyph-9nWc-KghkqS62flJh"),sQuery(id+"F0.wireOp",EDGE,"gJlDzY57-16t4-Vf8D-4nsT-QQv6MURsNHDC"),sQuery(id+"F0.wireOp",EDGE,"S4L2WrHO-g6c6-6cLC-dkaz-DY6cZUDI1iXS"),sQuery(id+"F0.wireOp",EDGE,"IIVYpRpw-wNBd-OXcb-W0MZ-mRHXIPyjJA5R"),sQuery(id+"F0.wireOp",EDGE,"wgGCBpVZ-QxlM-H5Bi-xMEc-6BhFhbDtORX5"),sQuery(id+"F0.wireOp",EDGE,"d3VJdfNO-Fk8P-fh5y-onYD-prEol703JRMM")])],"isStart":true})});
            var Q5;
            Q5=makeQuery(id+"F2.boolean.opBoolean","SPLIT",FACE,{"disambiguationData":[TD([makeQuery(id+"F2.opExtrude","SWEPT_FACE",FACE,{"disambiguationData":[OSD([sQuery(id+"F0.wireOp",EDGE,"E21.0")])]})])],"derivedFrom":makeQuery(id+"F1.opExtrude","CAP_FACE",FACE,{"disambiguationData":[OSD([sQuery(id+"F0.wireOp",EDGE,"E0.bottom"),sQuery(id+"F0.wireOp",EDGE,"E0.top"),sQuery(id+"F0.wireOp",EDGE,"E0.left"),sQuery(id+"F0.wireOp",EDGE,"E0.right"),sQuery(id+"F0.wireOp",EDGE,"E1.bottom"),sQuery(id+"F0.wireOp",EDGE,"E1.top"),sQuery(id+"F0.wireOp",EDGE,"E1.left"),sQuery(id+"F0.wireOp",EDGE,"E1.right"),sQuery(id+"F0.wireOp",EDGE,"E2.bottom"),sQuery(id+"F0.wireOp",EDGE,"E2.top"),sQuery(id+"F0.wireOp",EDGE,"E2.left"),sQuery(id+"F0.wireOp",EDGE,"E2.right"),sQuery(id+"F0.wireOp",EDGE,"E3.bottom"),sQuery(id+"F0.wireOp",EDGE,"E3.top"),sQuery(id+"F0.wireOp",EDGE,"E3.left"),sQuery(id+"F0.wireOp",EDGE,"E3.right"),sQuery(id+"F0.wireOp",EDGE,"E4.bottom"),sQuery(id+"F0.wireOp",EDGE,"E4.top"),sQuery(id+"F0.wireOp",EDGE,"E4.left"),sQuery(id+"F0.wireOp",EDGE,"E4.right"),sQuery(id+"F0.wireOp",EDGE,"E5.bottom"),sQuery(id+"F0.wireOp",EDGE,"E5.top"),sQuery(id+"F0.wireOp",EDGE,"E5.left"),sQuery(id+"F0.wireOp",EDGE,"E5.right"),sQuery(id+"F0.wireOp",EDGE,"cyoVeOsO-Ylvr-umjH-xySE-kTFhUaTDjDfD"),sQuery(id+"F0.wireOp",EDGE,"3eRy93ct-3uHp-ltHB-iF47-y57oyBoY3byI"),sQuery(id+"F0.wireOp",EDGE,"lrmn35il-Zq5m-sfIJ-5385-KA4XqFf2W20m"),sQuery(id+"F0.wireOp",EDGE,"QQd6hot7-zCFL-FVzE-QJR4-5pPOlfIRa5t9"),sQuery(id+"F0.wireOp",EDGE,"atnKaNye-AkJt-ZNtv-891p-w1etO83M4aAZ"),sQuery(id+"F0.wireOp",EDGE,"VlebEy6t-9yxg-sLxx-iXkv-Cso8guSqJYIt"),sQuery(id+"F0.wireOp",EDGE,"8PrGnW9D-uxJ0-gMwz-QmAr-Uvm73S1oeha5"),sQuery(id+"F0.wireOp",EDGE,"J0IPBTmc-wLEG-zjEr-TODg-CiZrFgkn9riR"),sQuery(id+"F0.wireOp",EDGE,"vcY6GDkU-c4bm-z2yD-HaH5-KhH9jC7oKOPS"),sQuery(id+"F0.wireOp",EDGE,"iaEsDPjX-zqyW-dyph-9nWc-KghkqS62flJh"),sQuery(id+"F0.wireOp",EDGE,"gJlDzY57-16t4-Vf8D-4nsT-QQv6MURsNHDC"),sQuery(id+"F0.wireOp",EDGE,"S4L2WrHO-g6c6-6cLC-dkaz-DY6cZUDI1iXS"),sQuery(id+"F0.wireOp",EDGE,"IIVYpRpw-wNBd-OXcb-W0MZ-mRHXIPyjJA5R"),sQuery(id+"F0.wireOp",EDGE,"wgGCBpVZ-QxlM-H5Bi-xMEc-6BhFhbDtORX5"),sQuery(id+"F0.wireOp",EDGE,"d3VJdfNO-Fk8P-fh5y-onYD-prEol703JRMM")])],"isStart":true})});
            var Q6;
            Q6=makeQuery(id+"F2.boolean.opBoolean","SPLIT",FACE,{"disambiguationData":[TD([makeQuery(id+"F2.opExtrude","SWEPT_FACE",FACE,{"disambiguationData":[OSD([sQuery(id+"F0.wireOp",EDGE,"E20.0")])]})])],"derivedFrom":makeQuery(id+"F1.opExtrude","CAP_FACE",FACE,{"disambiguationData":[OSD([sQuery(id+"F0.wireOp",EDGE,"E0.bottom"),sQuery(id+"F0.wireOp",EDGE,"E0.top"),sQuery(id+"F0.wireOp",EDGE,"E0.left"),sQuery(id+"F0.wireOp",EDGE,"E0.right"),sQuery(id+"F0.wireOp",EDGE,"E1.bottom"),sQuery(id+"F0.wireOp",EDGE,"E1.top"),sQuery(id+"F0.wireOp",EDGE,"E1.left"),sQuery(id+"F0.wireOp",EDGE,"E1.right"),sQuery(id+"F0.wireOp",EDGE,"E2.bottom"),sQuery(id+"F0.wireOp",EDGE,"E2.top"),sQuery(id+"F0.wireOp",EDGE,"E2.left"),sQuery(id+"F0.wireOp",EDGE,"E2.right"),sQuery(id+"F0.wireOp",EDGE,"E3.bottom"),sQuery(id+"F0.wireOp",EDGE,"E3.top"),sQuery(id+"F0.wireOp",EDGE,"E3.left"),sQuery(id+"F0.wireOp",EDGE,"E3.right"),sQuery(id+"F0.wireOp",EDGE,"E4.bottom"),sQuery(id+"F0.wireOp",EDGE,"E4.top"),sQuery(id+"F0.wireOp",EDGE,"E4.left"),sQuery(id+"F0.wireOp",EDGE,"E4.right"),sQuery(id+"F0.wireOp",EDGE,"E5.bottom"),sQuery(id+"F0.wireOp",EDGE,"E5.top"),sQuery(id+"F0.wireOp",EDGE,"E5.left"),sQuery(id+"F0.wireOp",EDGE,"E5.right"),sQuery(id+"F0.wireOp",EDGE,"cyoVeOsO-Ylvr-umjH-xySE-kTFhUaTDjDfD"),sQuery(id+"F0.wireOp",EDGE,"3eRy93ct-3uHp-ltHB-iF47-y57oyBoY3byI"),sQuery(id+"F0.wireOp",EDGE,"lrmn35il-Zq5m-sfIJ-5385-KA4XqFf2W20m"),sQuery(id+"F0.wireOp",EDGE,"QQd6hot7-zCFL-FVzE-QJR4-5pPOlfIRa5t9"),sQuery(id+"F0.wireOp",EDGE,"atnKaNye-AkJt-ZNtv-891p-w1etO83M4aAZ"),sQuery(id+"F0.wireOp",EDGE,"VlebEy6t-9yxg-sLxx-iXkv-Cso8guSqJYIt"),sQuery(id+"F0.wireOp",EDGE,"8PrGnW9D-uxJ0-gMwz-QmAr-Uvm73S1oeha5"),sQuery(id+"F0.wireOp",EDGE,"J0IPBTmc-wLEG-zjEr-TODg-CiZrFgkn9riR"),sQuery(id+"F0.wireOp",EDGE,"vcY6GDkU-c4bm-z2yD-HaH5-KhH9jC7oKOPS"),sQuery(id+"F0.wireOp",EDGE,"iaEsDPjX-zqyW-dyph-9nWc-KghkqS62flJh"),sQuery(id+"F0.wireOp",EDGE,"gJlDzY57-16t4-Vf8D-4nsT-QQv6MURsNHDC"),sQuery(id+"F0.wireOp",EDGE,"S4L2WrHO-g6c6-6cLC-dkaz-DY6cZUDI1iXS"),sQuery(id+"F0.wireOp",EDGE,"IIVYpRpw-wNBd-OXcb-W0MZ-mRHXIPyjJA5R"),sQuery(id+"F0.wireOp",EDGE,"wgGCBpVZ-QxlM-H5Bi-xMEc-6BhFhbDtORX5"),sQuery(id+"F0.wireOp",EDGE,"d3VJdfNO-Fk8P-fh5y-onYD-prEol703JRMM")])],"isStart":true})});
            var Q7;
            Q7=makeQuery(id+"F2.boolean.opBoolean","SPLIT",FACE,{"disambiguationData":[TD([makeQuery(id+"F2.opExtrude","SWEPT_FACE",FACE,{"disambiguationData":[OSD([sQuery(id+"F0.wireOp",EDGE,"E26.MirrorC")])]})])],"derivedFrom":makeQuery(id+"F1.opExtrude","CAP_FACE",FACE,{"disambiguationData":[OSD([sQuery(id+"F0.wireOp",EDGE,"E0.bottom"),sQuery(id+"F0.wireOp",EDGE,"E0.top"),sQuery(id+"F0.wireOp",EDGE,"E0.left"),sQuery(id+"F0.wireOp",EDGE,"E0.right"),sQuery(id+"F0.wireOp",EDGE,"E1.bottom"),sQuery(id+"F0.wireOp",EDGE,"E1.top"),sQuery(id+"F0.wireOp",EDGE,"E1.left"),sQuery(id+"F0.wireOp",EDGE,"E1.right"),sQuery(id+"F0.wireOp",EDGE,"E2.bottom"),sQuery(id+"F0.wireOp",EDGE,"E2.top"),sQuery(id+"F0.wireOp",EDGE,"E2.left"),sQuery(id+"F0.wireOp",EDGE,"E2.right"),sQuery(id+"F0.wireOp",EDGE,"E3.bottom"),sQuery(id+"F0.wireOp",EDGE,"E3.top"),sQuery(id+"F0.wireOp",EDGE,"E3.left"),sQuery(id+"F0.wireOp",EDGE,"E3.right"),sQuery(id+"F0.wireOp",EDGE,"E4.bottom"),sQuery(id+"F0.wireOp",EDGE,"E4.top"),sQuery(id+"F0.wireOp",EDGE,"E4.left"),sQuery(id+"F0.wireOp",EDGE,"E4.right"),sQuery(id+"F0.wireOp",EDGE,"E5.bottom"),sQuery(id+"F0.wireOp",EDGE,"E5.top"),sQuery(id+"F0.wireOp",EDGE,"E5.left"),sQuery(id+"F0.wireOp",EDGE,"E5.right"),sQuery(id+"F0.wireOp",EDGE,"cyoVeOsO-Ylvr-umjH-xySE-kTFhUaTDjDfD"),sQuery(id+"F0.wireOp",EDGE,"3eRy93ct-3uHp-ltHB-iF47-y57oyBoY3byI"),sQuery(id+"F0.wireOp",EDGE,"lrmn35il-Zq5m-sfIJ-5385-KA4XqFf2W20m"),sQuery(id+"F0.wireOp",EDGE,"QQd6hot7-zCFL-FVzE-QJR4-5pPOlfIRa5t9"),sQuery(id+"F0.wireOp",EDGE,"atnKaNye-AkJt-ZNtv-891p-w1etO83M4aAZ"),sQuery(id+"F0.wireOp",EDGE,"VlebEy6t-9yxg-sLxx-iXkv-Cso8guSqJYIt"),sQuery(id+"F0.wireOp",EDGE,"8PrGnW9D-uxJ0-gMwz-QmAr-Uvm73S1oeha5"),sQuery(id+"F0.wireOp",EDGE,"J0IPBTmc-wLEG-zjEr-TODg-CiZrFgkn9riR"),sQuery(id+"F0.wireOp",EDGE,"vcY6GDkU-c4bm-z2yD-HaH5-KhH9jC7oKOPS"),sQuery(id+"F0.wireOp",EDGE,"iaEsDPjX-zqyW-dyph-9nWc-KghkqS62flJh"),sQuery(id+"F0.wireOp",EDGE,"gJlDzY57-16t4-Vf8D-4nsT-QQv6MURsNHDC"),sQuery(id+"F0.wireOp",EDGE,"S4L2WrHO-g6c6-6cLC-dkaz-DY6cZUDI1iXS"),sQuery(id+"F0.wireOp",EDGE,"IIVYpRpw-wNBd-OXcb-W0MZ-mRHXIPyjJA5R"),sQuery(id+"F0.wireOp",EDGE,"wgGCBpVZ-QxlM-H5Bi-xMEc-6BhFhbDtORX5"),sQuery(id+"F0.wireOp",EDGE,"d3VJdfNO-Fk8P-fh5y-onYD-prEol703JRMM")])],"isStart":true})});
            var Q8;
            Q8=makeQuery(id+"F2.boolean.opBoolean","SPLIT",FACE,{"disambiguationData":[TD([makeQuery(id+"F2.opExtrude","SWEPT_FACE",FACE,{"disambiguationData":[OSD([sQuery(id+"F0.wireOp",EDGE,"E25.MirrorC")])]})])],"derivedFrom":makeQuery(id+"F1.opExtrude","CAP_FACE",FACE,{"disambiguationData":[OSD([sQuery(id+"F0.wireOp",EDGE,"E0.bottom"),sQuery(id+"F0.wireOp",EDGE,"E0.top"),sQuery(id+"F0.wireOp",EDGE,"E0.left"),sQuery(id+"F0.wireOp",EDGE,"E0.right"),sQuery(id+"F0.wireOp",EDGE,"E1.bottom"),sQuery(id+"F0.wireOp",EDGE,"E1.top"),sQuery(id+"F0.wireOp",EDGE,"E1.left"),sQuery(id+"F0.wireOp",EDGE,"E1.right"),sQuery(id+"F0.wireOp",EDGE,"E2.bottom"),sQuery(id+"F0.wireOp",EDGE,"E2.top"),sQuery(id+"F0.wireOp",EDGE,"E2.left"),sQuery(id+"F0.wireOp",EDGE,"E2.right"),sQuery(id+"F0.wireOp",EDGE,"E3.bottom"),sQuery(id+"F0.wireOp",EDGE,"E3.top"),sQuery(id+"F0.wireOp",EDGE,"E3.left"),sQuery(id+"F0.wireOp",EDGE,"E3.right"),sQuery(id+"F0.wireOp",EDGE,"E4.bottom"),sQuery(id+"F0.wireOp",EDGE,"E4.top"),sQuery(id+"F0.wireOp",EDGE,"E4.left"),sQuery(id+"F0.wireOp",EDGE,"E4.right"),sQuery(id+"F0.wireOp",EDGE,"E5.bottom"),sQuery(id+"F0.wireOp",EDGE,"E5.top"),sQuery(id+"F0.wireOp",EDGE,"E5.left"),sQuery(id+"F0.wireOp",EDGE,"E5.right"),sQuery(id+"F0.wireOp",EDGE,"cyoVeOsO-Ylvr-umjH-xySE-kTFhUaTDjDfD"),sQuery(id+"F0.wireOp",EDGE,"3eRy93ct-3uHp-ltHB-iF47-y57oyBoY3byI"),sQuery(id+"F0.wireOp",EDGE,"lrmn35il-Zq5m-sfIJ-5385-KA4XqFf2W20m"),sQuery(id+"F0.wireOp",EDGE,"QQd6hot7-zCFL-FVzE-QJR4-5pPOlfIRa5t9"),sQuery(id+"F0.wireOp",EDGE,"atnKaNye-AkJt-ZNtv-891p-w1etO83M4aAZ"),sQuery(id+"F0.wireOp",EDGE,"VlebEy6t-9yxg-sLxx-iXkv-Cso8guSqJYIt"),sQuery(id+"F0.wireOp",EDGE,"8PrGnW9D-uxJ0-gMwz-QmAr-Uvm73S1oeha5"),sQuery(id+"F0.wireOp",EDGE,"J0IPBTmc-wLEG-zjEr-TODg-CiZrFgkn9riR"),sQuery(id+"F0.wireOp",EDGE,"vcY6GDkU-c4bm-z2yD-HaH5-KhH9jC7oKOPS"),sQuery(id+"F0.wireOp",EDGE,"iaEsDPjX-zqyW-dyph-9nWc-KghkqS62flJh"),sQuery(id+"F0.wireOp",EDGE,"gJlDzY57-16t4-Vf8D-4nsT-QQv6MURsNHDC"),sQuery(id+"F0.wireOp",EDGE,"S4L2WrHO-g6c6-6cLC-dkaz-DY6cZUDI1iXS"),sQuery(id+"F0.wireOp",EDGE,"IIVYpRpw-wNBd-OXcb-W0MZ-mRHXIPyjJA5R"),sQuery(id+"F0.wireOp",EDGE,"wgGCBpVZ-QxlM-H5Bi-xMEc-6BhFhbDtORX5"),sQuery(id+"F0.wireOp",EDGE,"d3VJdfNO-Fk8P-fh5y-onYD-prEol703JRMM")])],"isStart":true})});
            var Q9;
            Q9=makeQuery(id+"F2.boolean.opBoolean","SPLIT",FACE,{"disambiguationData":[TD([makeQuery(id+"F2.opExtrude","SWEPT_FACE",FACE,{"disambiguationData":[OSD([sQuery(id+"F0.wireOp",EDGE,"E19.0")])]})])],"derivedFrom":makeQuery(id+"F1.opExtrude","CAP_FACE",FACE,{"disambiguationData":[OSD([sQuery(id+"F0.wireOp",EDGE,"E0.bottom"),sQuery(id+"F0.wireOp",EDGE,"E0.top"),sQuery(id+"F0.wireOp",EDGE,"E0.left"),sQuery(id+"F0.wireOp",EDGE,"E0.right"),sQuery(id+"F0.wireOp",EDGE,"E1.bottom"),sQuery(id+"F0.wireOp",EDGE,"E1.top"),sQuery(id+"F0.wireOp",EDGE,"E1.left"),sQuery(id+"F0.wireOp",EDGE,"E1.right"),sQuery(id+"F0.wireOp",EDGE,"E2.bottom"),sQuery(id+"F0.wireOp",EDGE,"E2.top"),sQuery(id+"F0.wireOp",EDGE,"E2.left"),sQuery(id+"F0.wireOp",EDGE,"E2.right"),sQuery(id+"F0.wireOp",EDGE,"E3.bottom"),sQuery(id+"F0.wireOp",EDGE,"E3.top"),sQuery(id+"F0.wireOp",EDGE,"E3.left"),sQuery(id+"F0.wireOp",EDGE,"E3.right"),sQuery(id+"F0.wireOp",EDGE,"E4.bottom"),sQuery(id+"F0.wireOp",EDGE,"E4.top"),sQuery(id+"F0.wireOp",EDGE,"E4.left"),sQuery(id+"F0.wireOp",EDGE,"E4.right"),sQuery(id+"F0.wireOp",EDGE,"E5.bottom"),sQuery(id+"F0.wireOp",EDGE,"E5.top"),sQuery(id+"F0.wireOp",EDGE,"E5.left"),sQuery(id+"F0.wireOp",EDGE,"E5.right"),sQuery(id+"F0.wireOp",EDGE,"cyoVeOsO-Ylvr-umjH-xySE-kTFhUaTDjDfD"),sQuery(id+"F0.wireOp",EDGE,"3eRy93ct-3uHp-ltHB-iF47-y57oyBoY3byI"),sQuery(id+"F0.wireOp",EDGE,"lrmn35il-Zq5m-sfIJ-5385-KA4XqFf2W20m"),sQuery(id+"F0.wireOp",EDGE,"QQd6hot7-zCFL-FVzE-QJR4-5pPOlfIRa5t9"),sQuery(id+"F0.wireOp",EDGE,"atnKaNye-AkJt-ZNtv-891p-w1etO83M4aAZ"),sQuery(id+"F0.wireOp",EDGE,"VlebEy6t-9yxg-sLxx-iXkv-Cso8guSqJYIt"),sQuery(id+"F0.wireOp",EDGE,"8PrGnW9D-uxJ0-gMwz-QmAr-Uvm73S1oeha5"),sQuery(id+"F0.wireOp",EDGE,"J0IPBTmc-wLEG-zjEr-TODg-CiZrFgkn9riR"),sQuery(id+"F0.wireOp",EDGE,"vcY6GDkU-c4bm-z2yD-HaH5-KhH9jC7oKOPS"),sQuery(id+"F0.wireOp",EDGE,"iaEsDPjX-zqyW-dyph-9nWc-KghkqS62flJh"),sQuery(id+"F0.wireOp",EDGE,"gJlDzY57-16t4-Vf8D-4nsT-QQv6MURsNHDC"),sQuery(id+"F0.wireOp",EDGE,"S4L2WrHO-g6c6-6cLC-dkaz-DY6cZUDI1iXS"),sQuery(id+"F0.wireOp",EDGE,"IIVYpRpw-wNBd-OXcb-W0MZ-mRHXIPyjJA5R"),sQuery(id+"F0.wireOp",EDGE,"wgGCBpVZ-QxlM-H5Bi-xMEc-6BhFhbDtORX5"),sQuery(id+"F0.wireOp",EDGE,"d3VJdfNO-Fk8P-fh5y-onYD-prEol703JRMM")])],"isStart":true})});
            var Q10;
            Q10=makeQuery(id+"F2.boolean.opBoolean","SPLIT",FACE,{"disambiguationData":[TD([makeQuery(id+"F2.opExtrude","SWEPT_FACE",FACE,{"disambiguationData":[OSD([sQuery(id+"F0.wireOp",EDGE,"E18.0")])]})])],"derivedFrom":makeQuery(id+"F1.opExtrude","CAP_FACE",FACE,{"disambiguationData":[OSD([sQuery(id+"F0.wireOp",EDGE,"E0.bottom"),sQuery(id+"F0.wireOp",EDGE,"E0.top"),sQuery(id+"F0.wireOp",EDGE,"E0.left"),sQuery(id+"F0.wireOp",EDGE,"E0.right"),sQuery(id+"F0.wireOp",EDGE,"E1.bottom"),sQuery(id+"F0.wireOp",EDGE,"E1.top"),sQuery(id+"F0.wireOp",EDGE,"E1.left"),sQuery(id+"F0.wireOp",EDGE,"E1.right"),sQuery(id+"F0.wireOp",EDGE,"E2.bottom"),sQuery(id+"F0.wireOp",EDGE,"E2.top"),sQuery(id+"F0.wireOp",EDGE,"E2.left"),sQuery(id+"F0.wireOp",EDGE,"E2.right"),sQuery(id+"F0.wireOp",EDGE,"E3.bottom"),sQuery(id+"F0.wireOp",EDGE,"E3.top"),sQuery(id+"F0.wireOp",EDGE,"E3.left"),sQuery(id+"F0.wireOp",EDGE,"E3.right"),sQuery(id+"F0.wireOp",EDGE,"E4.bottom"),sQuery(id+"F0.wireOp",EDGE,"E4.top"),sQuery(id+"F0.wireOp",EDGE,"E4.left"),sQuery(id+"F0.wireOp",EDGE,"E4.right"),sQuery(id+"F0.wireOp",EDGE,"E5.bottom"),sQuery(id+"F0.wireOp",EDGE,"E5.top"),sQuery(id+"F0.wireOp",EDGE,"E5.left"),sQuery(id+"F0.wireOp",EDGE,"E5.right"),sQuery(id+"F0.wireOp",EDGE,"cyoVeOsO-Ylvr-umjH-xySE-kTFhUaTDjDfD"),sQuery(id+"F0.wireOp",EDGE,"3eRy93ct-3uHp-ltHB-iF47-y57oyBoY3byI"),sQuery(id+"F0.wireOp",EDGE,"lrmn35il-Zq5m-sfIJ-5385-KA4XqFf2W20m"),sQuery(id+"F0.wireOp",EDGE,"QQd6hot7-zCFL-FVzE-QJR4-5pPOlfIRa5t9"),sQuery(id+"F0.wireOp",EDGE,"atnKaNye-AkJt-ZNtv-891p-w1etO83M4aAZ"),sQuery(id+"F0.wireOp",EDGE,"VlebEy6t-9yxg-sLxx-iXkv-Cso8guSqJYIt"),sQuery(id+"F0.wireOp",EDGE,"8PrGnW9D-uxJ0-gMwz-QmAr-Uvm73S1oeha5"),sQuery(id+"F0.wireOp",EDGE,"J0IPBTmc-wLEG-zjEr-TODg-CiZrFgkn9riR"),sQuery(id+"F0.wireOp",EDGE,"vcY6GDkU-c4bm-z2yD-HaH5-KhH9jC7oKOPS"),sQuery(id+"F0.wireOp",EDGE,"iaEsDPjX-zqyW-dyph-9nWc-KghkqS62flJh"),sQuery(id+"F0.wireOp",EDGE,"gJlDzY57-16t4-Vf8D-4nsT-QQv6MURsNHDC"),sQuery(id+"F0.wireOp",EDGE,"S4L2WrHO-g6c6-6cLC-dkaz-DY6cZUDI1iXS"),sQuery(id+"F0.wireOp",EDGE,"IIVYpRpw-wNBd-OXcb-W0MZ-mRHXIPyjJA5R"),sQuery(id+"F0.wireOp",EDGE,"wgGCBpVZ-QxlM-H5Bi-xMEc-6BhFhbDtORX5"),sQuery(id+"F0.wireOp",EDGE,"d3VJdfNO-Fk8P-fh5y-onYD-prEol703JRMM")])],"isStart":true})});
            var Q11;
            Q11=makeQuery(id+"F2.boolean.opBoolean","SPLIT",FACE,{"disambiguationData":[TD([makeQuery(id+"F2.opExtrude","SWEPT_FACE",FACE,{"disambiguationData":[OSD([sQuery(id+"F0.wireOp",EDGE,"E24.MirrorC")])]})])],"derivedFrom":makeQuery(id+"F1.opExtrude","CAP_FACE",FACE,{"disambiguationData":[OSD([sQuery(id+"F0.wireOp",EDGE,"E0.bottom"),sQuery(id+"F0.wireOp",EDGE,"E0.top"),sQuery(id+"F0.wireOp",EDGE,"E0.left"),sQuery(id+"F0.wireOp",EDGE,"E0.right"),sQuery(id+"F0.wireOp",EDGE,"E1.bottom"),sQuery(id+"F0.wireOp",EDGE,"E1.top"),sQuery(id+"F0.wireOp",EDGE,"E1.left"),sQuery(id+"F0.wireOp",EDGE,"E1.right"),sQuery(id+"F0.wireOp",EDGE,"E2.bottom"),sQuery(id+"F0.wireOp",EDGE,"E2.top"),sQuery(id+"F0.wireOp",EDGE,"E2.left"),sQuery(id+"F0.wireOp",EDGE,"E2.right"),sQuery(id+"F0.wireOp",EDGE,"E3.bottom"),sQuery(id+"F0.wireOp",EDGE,"E3.top"),sQuery(id+"F0.wireOp",EDGE,"E3.left"),sQuery(id+"F0.wireOp",EDGE,"E3.right"),sQuery(id+"F0.wireOp",EDGE,"E4.bottom"),sQuery(id+"F0.wireOp",EDGE,"E4.top"),sQuery(id+"F0.wireOp",EDGE,"E4.left"),sQuery(id+"F0.wireOp",EDGE,"E4.right"),sQuery(id+"F0.wireOp",EDGE,"E5.bottom"),sQuery(id+"F0.wireOp",EDGE,"E5.top"),sQuery(id+"F0.wireOp",EDGE,"E5.left"),sQuery(id+"F0.wireOp",EDGE,"E5.right"),sQuery(id+"F0.wireOp",EDGE,"cyoVeOsO-Ylvr-umjH-xySE-kTFhUaTDjDfD"),sQuery(id+"F0.wireOp",EDGE,"3eRy93ct-3uHp-ltHB-iF47-y57oyBoY3byI"),sQuery(id+"F0.wireOp",EDGE,"lrmn35il-Zq5m-sfIJ-5385-KA4XqFf2W20m"),sQuery(id+"F0.wireOp",EDGE,"QQd6hot7-zCFL-FVzE-QJR4-5pPOlfIRa5t9"),sQuery(id+"F0.wireOp",EDGE,"atnKaNye-AkJt-ZNtv-891p-w1etO83M4aAZ"),sQuery(id+"F0.wireOp",EDGE,"VlebEy6t-9yxg-sLxx-iXkv-Cso8guSqJYIt"),sQuery(id+"F0.wireOp",EDGE,"8PrGnW9D-uxJ0-gMwz-QmAr-Uvm73S1oeha5"),sQuery(id+"F0.wireOp",EDGE,"J0IPBTmc-wLEG-zjEr-TODg-CiZrFgkn9riR"),sQuery(id+"F0.wireOp",EDGE,"vcY6GDkU-c4bm-z2yD-HaH5-KhH9jC7oKOPS"),sQuery(id+"F0.wireOp",EDGE,"iaEsDPjX-zqyW-dyph-9nWc-KghkqS62flJh"),sQuery(id+"F0.wireOp",EDGE,"gJlDzY57-16t4-Vf8D-4nsT-QQv6MURsNHDC"),sQuery(id+"F0.wireOp",EDGE,"S4L2WrHO-g6c6-6cLC-dkaz-DY6cZUDI1iXS"),sQuery(id+"F0.wireOp",EDGE,"IIVYpRpw-wNBd-OXcb-W0MZ-mRHXIPyjJA5R"),sQuery(id+"F0.wireOp",EDGE,"wgGCBpVZ-QxlM-H5Bi-xMEc-6BhFhbDtORX5"),sQuery(id+"F0.wireOp",EDGE,"d3VJdfNO-Fk8P-fh5y-onYD-prEol703JRMM")])],"isStart":true})});
            extrude(context, id + "F5", {"entities" : qUnion([Q0, Q1, Q2, Q3, Q4, Q5, Q6, Q7, Q8, Q9, Q10, Q11]), "operationType" : NewBodyOperationType.REMOVE, "oppositeDirection" : true, "depth" : 0.9 * mm, "offsetDistance" : 25 * mm});
        }
        {
            var Q0;
            Q0=qCreatedBy(makeId("Top.planeOp"),FACE);
            cPlane(context, id + "F6", {"entities" : qUnion([Q0]), "cplaneType" : CPlaneType.OFFSET, "offset" : 8.7 * mm, "oppositeDirection" : true, "width" : 150 * mm, "height" : 150 * mm});
        }
        {
            var Q0;
            Q0=qCreatedBy(id+"F6.planeOp",FACE);
            var sketch = newSketch(context, id + "F7", { "sketchPlane" : qUnion([Q0])});
            skCircle(sketch, "E59", {"center": v(0, 0) * mm, "radius": 0.25 * mm, "construction": true});
            skLineSegment(sketch, "E60", {"start": v(-25.8, 2.68) * mm, "end": v(-21.4, 2.68) * mm, "construction": true});
            skLineSegment(sketch, "E61", {"start": v(25.8, 2.68) * mm, "end": v(21.4, 2.68) * mm, "construction": true});
            skLineSegment(sketch, "E62", {"start": v(14, 2.68) * mm, "end": v(9.6, 2.68) * mm, "construction": true});
            skLineSegment(sketch, "E63", {"start": v(2.2, 2.68) * mm, "end": v(-2.2, 2.68) * mm, "construction": true});
            skLineSegment(sketch, "E64", {"start": v(-9.6, 2.68) * mm, "end": v(-14, 2.68) * mm, "construction": true});
            skCircle(sketch, "E65", {"center": v(-23.6, 0) * mm, "radius": 2.2 * mm, "construction": true});
            skCircle(sketch, "E66", {"center": v(-11.8, 0) * mm, "radius": 2.2 * mm, "construction": true});
            skCircle(sketch, "E67", {"center": v(0, 0) * mm, "radius": 2.2 * mm, "construction": true});
            skCircle(sketch, "E68", {"center": v(11.8, 0) * mm, "radius": 2.2 * mm, "construction": true});
            skCircle(sketch, "E69", {"center": v(23.6, 0) * mm, "radius": 2.2 * mm, "construction": true});
            skLineSegment(sketch, "E70.bottom", {"start": v(35, -11) * mm, "end": v(-35, -11) * mm});
            skLineSegment(sketch, "E70.top", {"start": v(35, 11) * mm, "end": v(-35, 11) * mm});
            skLineSegment(sketch, "E70.left", {"start": v(35, -11) * mm, "end": v(35, 11) * mm});
            skLineSegment(sketch, "E70.right", {"start": v(-35, -11) * mm, "end": v(-35, 11) * mm});
            skLineSegment(sketch, "E71", {"start": v(-25.8, 8.5) * mm, "end": v(-21.4, 8.5) * mm, "construction": true});
            skLineSegment(sketch, "E72", {"start": v(-14, 8.5) * mm, "end": v(-9.6, 8.5) * mm, "construction": true});
            skLineSegment(sketch, "E73", {"start": v(-2.2, 8.5) * mm, "end": v(2.2, 8.5) * mm, "construction": true});
            skLineSegment(sketch, "E74", {"start": v(9.6, 8.5) * mm, "end": v(14, 8.5) * mm, "construction": true});
            skLineSegment(sketch, "E75", {"start": v(21.4, 8.5) * mm, "end": v(25.8, 8.5) * mm, "construction": true});
            skLineSegment(sketch, "E76.trimOffspring", {"start": v(-25.8, 2.68) * mm, "end": v(-25.8, 8.5) * mm, "construction": true});
            skLineSegment(sketch, "E77.trimOffspring", {"start": v(-21.4, 2.68) * mm, "end": v(-21.4, 8.5) * mm, "construction": true});
            skLineSegment(sketch, "E78.trimOffspring", {"start": v(-14, 2.68) * mm, "end": v(-14, 8.5) * mm, "construction": true});
            skLineSegment(sketch, "E79.trimOffspring", {"start": v(-9.6, 2.68) * mm, "end": v(-9.6, 8.5) * mm, "construction": true});
            skLineSegment(sketch, "E80.trimOffspring", {"start": v(-2.2, 2.68) * mm, "end": v(-2.2, 8.5) * mm, "construction": true});
            skLineSegment(sketch, "E81.trimOffspring", {"start": v(2.2, 2.68) * mm, "end": v(2.2, 8.5) * mm, "construction": true});
            skLineSegment(sketch, "E82.trimOffspring", {"start": v(9.6, 2.68) * mm, "end": v(9.6, 8.5) * mm, "construction": true});
            skLineSegment(sketch, "E83.trimOffspring", {"start": v(14, 2.68) * mm, "end": v(14, 8.5) * mm, "construction": true});
            skLineSegment(sketch, "E84.trimOffspring", {"start": v(21.4, 2.68) * mm, "end": v(21.4, 8.5) * mm, "construction": true});
            skLineSegment(sketch, "E85.trimOffspring", {"start": v(25.8, 2.68) * mm, "end": v(25.8, 8.5) * mm, "construction": true});
            skLineSegment(sketch, "E86.0", {"start": v(-25.5, 2.98) * mm, "end": v(-25.5, 8.2) * mm});
            skLineSegment(sketch, "E86.1", {"start": v(-25.5, 2.98) * mm, "end": v(-21.7, 2.98) * mm});
            skLineSegment(sketch, "E86.2", {"start": v(-21.7, 2.98) * mm, "end": v(-21.7, 8.2) * mm});
            skLineSegment(sketch, "E86.3", {"start": v(-25.5, 8.2) * mm, "end": v(-21.7, 8.2) * mm});
            skLineSegment(sketch, "E87.0", {"start": v(-13.7, 8.2) * mm, "end": v(-9.9, 8.2) * mm});
            skLineSegment(sketch, "E87.1", {"start": v(-13.7, 2.98) * mm, "end": v(-13.7, 8.2) * mm});
            skLineSegment(sketch, "E87.2", {"start": v(-9.9, 2.98) * mm, "end": v(-13.7, 2.98) * mm});
            skLineSegment(sketch, "E87.3", {"start": v(-9.9, 2.98) * mm, "end": v(-9.9, 8.2) * mm});
            skLineSegment(sketch, "E88.0", {"start": v(1.9, 2.98) * mm, "end": v(1.9, 8.2) * mm});
            skLineSegment(sketch, "E88.1", {"start": v(1.9, 2.98) * mm, "end": v(-1.9, 2.98) * mm});
            skLineSegment(sketch, "E88.2", {"start": v(-1.9, 2.98) * mm, "end": v(-1.9, 8.2) * mm});
            skLineSegment(sketch, "E88.3", {"start": v(-1.9, 8.2) * mm, "end": v(1.9, 8.2) * mm});
            skLineSegment(sketch, "E89.0", {"start": v(9.9, 2.98) * mm, "end": v(9.9, 8.2) * mm});
            skLineSegment(sketch, "E89.1", {"start": v(13.7, 2.98) * mm, "end": v(9.9, 2.98) * mm});
            skLineSegment(sketch, "E89.2", {"start": v(13.7, 2.98) * mm, "end": v(13.7, 8.2) * mm});
            skLineSegment(sketch, "E89.3", {"start": v(9.9, 8.2) * mm, "end": v(13.7, 8.2) * mm});
            skLineSegment(sketch, "E90.0", {"start": v(25.5, 2.98) * mm, "end": v(21.7, 2.98) * mm});
            skLineSegment(sketch, "E90.1", {"start": v(25.5, 2.98) * mm, "end": v(25.5, 8.2) * mm});
            skLineSegment(sketch, "E90.2", {"start": v(21.7, 8.2) * mm, "end": v(25.5, 8.2) * mm});
            skLineSegment(sketch, "E90.3", {"start": v(21.7, 2.98) * mm, "end": v(21.7, 8.2) * mm});
            skLineSegment(sketch, "E91", {"start": v(-35, 0) * mm, "end": v(35, 0) * mm, "construction": true});
            skCircle(sketch, "E92.0", {"center": v(-23.6, 0) * mm, "radius": 1.9 * mm});
            skCircle(sketch, "E93.0", {"center": v(-11.8, 0) * mm, "radius": 1.9 * mm});
            skCircle(sketch, "E94.0", {"center": v(0, 0) * mm, "radius": 1.9 * mm});
            skCircle(sketch, "E95.0", {"center": v(11.8, 0) * mm, "radius": 1.9 * mm});
            skCircle(sketch, "E96.0", {"center": v(23.6, 0) * mm, "radius": 1.9 * mm});
            skLineSegment(sketch, "E97.MirrorCS", {"start": v(25.8, -2.68) * mm, "end": v(25.8, -8.5) * mm, "construction": true});
            skLineSegment(sketch, "E98.MirrorCS", {"start": v(-25.5, -2.98) * mm, "end": v(-21.7, -2.98) * mm});
            skLineSegment(sketch, "E99.MirrorCS", {"start": v(-14, -8.5) * mm, "end": v(-9.6, -8.5) * mm, "construction": true});
            skLineSegment(sketch, "E100.MirrorCS", {"start": v(-13.7, -8.2) * mm, "end": v(-9.9, -8.2) * mm});
            skLineSegment(sketch, "E101.MirrorCS", {"start": v(-25.8, -2.68) * mm, "end": v(-21.4, -2.68) * mm, "construction": true});
            skLineSegment(sketch, "E102.MirrorCS", {"start": v(-1.9, -2.98) * mm, "end": v(-1.9, -8.2) * mm});
            skLineSegment(sketch, "E103.MirrorCS", {"start": v(21.4, -2.68) * mm, "end": v(21.4, -8.5) * mm, "construction": true});
            skLineSegment(sketch, "E104.MirrorCS", {"start": v(-2.2, -8.5) * mm, "end": v(2.2, -8.5) * mm, "construction": true});
            skLineSegment(sketch, "E105.MirrorCS", {"start": v(21.7, -8.2) * mm, "end": v(25.5, -8.2) * mm});
            skLineSegment(sketch, "E106.MirrorCS", {"start": v(9.6, -2.68) * mm, "end": v(9.6, -8.5) * mm, "construction": true});
            skLineSegment(sketch, "E107.MirrorCS", {"start": v(-13.7, -2.98) * mm, "end": v(-13.7, -8.2) * mm});
            skLineSegment(sketch, "E108.MirrorCS", {"start": v(13.7, -2.98) * mm, "end": v(13.7, -8.2) * mm});
            skLineSegment(sketch, "E109.MirrorCS", {"start": v(14, -2.68) * mm, "end": v(9.6, -2.68) * mm, "construction": true});
            skLineSegment(sketch, "E110.MirrorCS", {"start": v(-2.2, -2.68) * mm, "end": v(-2.2, -8.5) * mm, "construction": true});
            skLineSegment(sketch, "E111.MirrorCS", {"start": v(-25.8, -2.68) * mm, "end": v(-25.8, -8.5) * mm, "construction": true});
            skLineSegment(sketch, "E112.MirrorCS", {"start": v(1.9, -2.98) * mm, "end": v(-1.9, -2.98) * mm});
            skLineSegment(sketch, "E113.MirrorCS", {"start": v(9.9, -8.2) * mm, "end": v(13.7, -8.2) * mm});
            skLineSegment(sketch, "E114.MirrorCS", {"start": v(25.5, -2.98) * mm, "end": v(21.7, -2.98) * mm});
            skLineSegment(sketch, "E115.MirrorCS", {"start": v(9.6, -8.5) * mm, "end": v(14, -8.5) * mm, "construction": true});
            skLineSegment(sketch, "E116.MirrorCS", {"start": v(14, -2.68) * mm, "end": v(14, -8.5) * mm, "construction": true});
            skLineSegment(sketch, "E117.MirrorCS", {"start": v(-25.5, -8.2) * mm, "end": v(-21.7, -8.2) * mm});
            skLineSegment(sketch, "E118.MirrorCS", {"start": v(-21.4, -2.68) * mm, "end": v(-21.4, -8.5) * mm, "construction": true});
            skLineSegment(sketch, "E119.MirrorCS", {"start": v(25.5, -2.98) * mm, "end": v(25.5, -8.2) * mm});
            skLineSegment(sketch, "E120.MirrorCS", {"start": v(25.8, -2.68) * mm, "end": v(21.4, -2.68) * mm, "construction": true});
            skLineSegment(sketch, "E121.MirrorCS", {"start": v(21.7, -2.98) * mm, "end": v(21.7, -8.2) * mm});
            skLineSegment(sketch, "E122.MirrorCS", {"start": v(-9.9, -2.98) * mm, "end": v(-13.7, -2.98) * mm});
            skLineSegment(sketch, "E123.MirrorCS", {"start": v(-14, -2.68) * mm, "end": v(-14, -8.5) * mm, "construction": true});
            skLineSegment(sketch, "E124.MirrorCS", {"start": v(1.9, -2.98) * mm, "end": v(1.9, -8.2) * mm});
            skLineSegment(sketch, "E125.MirrorCS", {"start": v(21.4, -8.5) * mm, "end": v(25.8, -8.5) * mm, "construction": true});
            skLineSegment(sketch, "E126.MirrorCS", {"start": v(-25.8, -8.5) * mm, "end": v(-21.4, -8.5) * mm, "construction": true});
            skLineSegment(sketch, "E127.MirrorCS", {"start": v(2.2, -2.68) * mm, "end": v(-2.2, -2.68) * mm, "construction": true});
            skLineSegment(sketch, "E128.MirrorCS", {"start": v(-21.7, -2.98) * mm, "end": v(-21.7, -8.2) * mm});
            skLineSegment(sketch, "E129.MirrorCS", {"start": v(-9.9, -2.98) * mm, "end": v(-9.9, -8.2) * mm});
            skLineSegment(sketch, "E130.MirrorCS", {"start": v(-25.5, -2.98) * mm, "end": v(-25.5, -8.2) * mm});
            skLineSegment(sketch, "E131.MirrorCS", {"start": v(-1.9, -8.2) * mm, "end": v(1.9, -8.2) * mm});
            skLineSegment(sketch, "E132.MirrorCS", {"start": v(2.2, -2.68) * mm, "end": v(2.2, -8.5) * mm, "construction": true});
            skLineSegment(sketch, "E133.MirrorCS", {"start": v(-9.6, -2.68) * mm, "end": v(-14, -2.68) * mm, "construction": true});
            skLineSegment(sketch, "E134.MirrorCS", {"start": v(-9.6, -2.68) * mm, "end": v(-9.6, -8.5) * mm, "construction": true});
            skLineSegment(sketch, "E135.MirrorCS", {"start": v(9.9, -2.98) * mm, "end": v(9.9, -8.2) * mm});
            skLineSegment(sketch, "E136.MirrorCS", {"start": v(13.7, -2.98) * mm, "end": v(9.9, -2.98) * mm});
            skSolve(sketch);
        }
        {
            var Q0;
            Q0=makeQuery(id+"F7.imprint","IMPRINT",FACE,{"disambiguationData":[TD([[makeQuery(id+"F7.imprint","IMPRINT",EDGE,{"derivedFrom":sQuery(id+"F7.wireOp",EDGE,"E70.bottom")}),-1.0]])]});
            var Q1;
            Q1=makeQuery(id+"F7.imprint","IMPRINT",FACE,{"disambiguationData":[TD([[makeQuery(id+"F7.imprint","IMPRINT",EDGE,{"derivedFrom":sQuery(id+"F7.wireOp",EDGE,"E98.MirrorCS")}),-1.0]])]});
            var Q2;
            Q2=makeQuery(id+"F7.imprint","IMPRINT",FACE,{"disambiguationData":[TD([[makeQuery(id+"F7.imprint","IMPRINT",EDGE,{"derivedFrom":sQuery(id+"F7.wireOp",EDGE,"E92.0")}),1.0]])]});
            var Q3;
            Q3=makeQuery(id+"F7.imprint","IMPRINT",FACE,{"disambiguationData":[TD([[makeQuery(id+"F7.imprint","IMPRINT",EDGE,{"derivedFrom":sQuery(id+"F7.wireOp",EDGE,"E86.0")}),-1.0]])]});
            var Q4;
            Q4=makeQuery(id+"F7.imprint","IMPRINT",FACE,{"disambiguationData":[TD([[makeQuery(id+"F7.imprint","IMPRINT",EDGE,{"derivedFrom":sQuery(id+"F7.wireOp",EDGE,"E87.0")}),-1.0]])]});
            var Q5;
            Q5=makeQuery(id+"F7.imprint","IMPRINT",FACE,{"disambiguationData":[TD([[makeQuery(id+"F7.imprint","IMPRINT",EDGE,{"derivedFrom":sQuery(id+"F7.wireOp",EDGE,"E93.0")}),1.0]])]});
            var Q6;
            Q6=makeQuery(id+"F7.imprint","IMPRINT",FACE,{"disambiguationData":[TD([[makeQuery(id+"F7.imprint","IMPRINT",EDGE,{"derivedFrom":sQuery(id+"F7.wireOp",EDGE,"E100.MirrorCS")}),1.0]])]});
            var Q7;
            Q7=makeQuery(id+"F7.imprint","IMPRINT",FACE,{"disambiguationData":[TD([[makeQuery(id+"F7.imprint","IMPRINT",EDGE,{"derivedFrom":sQuery(id+"F7.wireOp",EDGE,"E102.MirrorCS")}),1.0]])]});
            var Q8;
            Q8=makeQuery(id+"F7.imprint","IMPRINT",FACE,{"disambiguationData":[TD([[makeQuery(id+"F7.imprint","IMPRINT",EDGE,{"derivedFrom":sQuery(id+"F7.wireOp",EDGE,"E88.0")}),1.0]])]});
            var Q9;
            Q9=makeQuery(id+"F7.imprint","IMPRINT",FACE,{"disambiguationData":[TD([[makeQuery(id+"F7.imprint","IMPRINT",EDGE,{"derivedFrom":sQuery(id+"F7.wireOp",EDGE,"E94.0")}),1.0]])]});
            var Q10;
            Q10=makeQuery(id+"F7.imprint","IMPRINT",FACE,{"disambiguationData":[TD([[makeQuery(id+"F7.imprint","IMPRINT",EDGE,{"derivedFrom":sQuery(id+"F7.wireOp",EDGE,"E95.0")}),1.0]])]});
            var Q11;
            Q11=makeQuery(id+"F7.imprint","IMPRINT",FACE,{"disambiguationData":[TD([[makeQuery(id+"F7.imprint","IMPRINT",EDGE,{"derivedFrom":sQuery(id+"F7.wireOp",EDGE,"E89.0")}),-1.0]])]});
            var Q12;
            Q12=makeQuery(id+"F7.imprint","IMPRINT",FACE,{"disambiguationData":[TD([[makeQuery(id+"F7.imprint","IMPRINT",EDGE,{"derivedFrom":sQuery(id+"F7.wireOp",EDGE,"E108.MirrorCS")}),-1.0]])]});
            var Q13;
            Q13=makeQuery(id+"F7.imprint","IMPRINT",FACE,{"disambiguationData":[TD([[makeQuery(id+"F7.imprint","IMPRINT",EDGE,{"derivedFrom":sQuery(id+"F7.wireOp",EDGE,"E105.MirrorCS")}),1.0]])]});
            var Q14;
            Q14=makeQuery(id+"F7.imprint","IMPRINT",FACE,{"disambiguationData":[TD([[makeQuery(id+"F7.imprint","IMPRINT",EDGE,{"derivedFrom":sQuery(id+"F7.wireOp",EDGE,"E96.0")}),1.0]])]});
            var Q15;
            Q15=makeQuery(id+"F7.imprint","IMPRINT",FACE,{"disambiguationData":[TD([[makeQuery(id+"F7.imprint","IMPRINT",EDGE,{"derivedFrom":sQuery(id+"F7.wireOp",EDGE,"E90.0")}),-1.0]])]});
            extrude(context, id + "F8", {"entities" : qUnion([Q0, Q1, Q2, Q3, Q4, Q5, Q6, Q7, Q8, Q9, Q10, Q11, Q12, Q13, Q14, Q15]), "oppositeDirection" : true, "depth" : 0.5 * mm, "offsetDistance" : 25 * mm});
        }
        {
            var Q0;
            Q0=makeQuery(id+"F7.imprint","IMPRINT",FACE,{"disambiguationData":[TD([[makeQuery(id+"F7.imprint","IMPRINT",EDGE,{"derivedFrom":sQuery(id+"F7.wireOp",EDGE,"E86.0")}),-1.0]])]});
            var Q1;
            Q1=makeQuery(id+"F7.imprint","IMPRINT",FACE,{"disambiguationData":[TD([[makeQuery(id+"F7.imprint","IMPRINT",EDGE,{"derivedFrom":sQuery(id+"F7.wireOp",EDGE,"E92.0")}),1.0]])]});
            var Q2;
            Q2=makeQuery(id+"F7.imprint","IMPRINT",FACE,{"disambiguationData":[TD([[makeQuery(id+"F7.imprint","IMPRINT",EDGE,{"derivedFrom":sQuery(id+"F7.wireOp",EDGE,"E98.MirrorCS")}),-1.0]])]});
            var Q3;
            Q3=makeQuery(id+"F7.imprint","IMPRINT",FACE,{"disambiguationData":[TD([[makeQuery(id+"F7.imprint","IMPRINT",EDGE,{"derivedFrom":sQuery(id+"F7.wireOp",EDGE,"E87.0")}),-1.0]])]});
            var Q4;
            Q4=makeQuery(id+"F7.imprint","IMPRINT",FACE,{"disambiguationData":[TD([[makeQuery(id+"F7.imprint","IMPRINT",EDGE,{"derivedFrom":sQuery(id+"F7.wireOp",EDGE,"E93.0")}),1.0]])]});
            var Q5;
            Q5=makeQuery(id+"F7.imprint","IMPRINT",FACE,{"disambiguationData":[TD([[makeQuery(id+"F7.imprint","IMPRINT",EDGE,{"derivedFrom":sQuery(id+"F7.wireOp",EDGE,"E100.MirrorCS")}),1.0]])]});
            var Q6;
            Q6=makeQuery(id+"F7.imprint","IMPRINT",FACE,{"disambiguationData":[TD([[makeQuery(id+"F7.imprint","IMPRINT",EDGE,{"derivedFrom":sQuery(id+"F7.wireOp",EDGE,"E88.0")}),1.0]])]});
            var Q7;
            Q7=makeQuery(id+"F7.imprint","IMPRINT",FACE,{"disambiguationData":[TD([[makeQuery(id+"F7.imprint","IMPRINT",EDGE,{"derivedFrom":sQuery(id+"F7.wireOp",EDGE,"E94.0")}),1.0]])]});
            var Q8;
            Q8=makeQuery(id+"F7.imprint","IMPRINT",FACE,{"disambiguationData":[TD([[makeQuery(id+"F7.imprint","IMPRINT",EDGE,{"derivedFrom":sQuery(id+"F7.wireOp",EDGE,"E102.MirrorCS")}),1.0]])]});
            var Q9;
            Q9=makeQuery(id+"F7.imprint","IMPRINT",FACE,{"disambiguationData":[TD([[makeQuery(id+"F7.imprint","IMPRINT",EDGE,{"derivedFrom":sQuery(id+"F7.wireOp",EDGE,"E89.0")}),-1.0]])]});
            var Q10;
            Q10=makeQuery(id+"F7.imprint","IMPRINT",FACE,{"disambiguationData":[TD([[makeQuery(id+"F7.imprint","IMPRINT",EDGE,{"derivedFrom":sQuery(id+"F7.wireOp",EDGE,"E95.0")}),1.0]])]});
            var Q11;
            Q11=makeQuery(id+"F7.imprint","IMPRINT",FACE,{"disambiguationData":[TD([[makeQuery(id+"F7.imprint","IMPRINT",EDGE,{"derivedFrom":sQuery(id+"F7.wireOp",EDGE,"E108.MirrorCS")}),-1.0]])]});
            var Q12;
            Q12=makeQuery(id+"F7.imprint","IMPRINT",FACE,{"disambiguationData":[TD([[makeQuery(id+"F7.imprint","IMPRINT",EDGE,{"derivedFrom":sQuery(id+"F7.wireOp",EDGE,"E90.0")}),-1.0]])]});
            var Q13;
            Q13=makeQuery(id+"F7.imprint","IMPRINT",FACE,{"disambiguationData":[TD([[makeQuery(id+"F7.imprint","IMPRINT",EDGE,{"derivedFrom":sQuery(id+"F7.wireOp",EDGE,"E96.0")}),1.0]])]});
            var Q14;
            Q14=makeQuery(id+"F7.imprint","IMPRINT",FACE,{"disambiguationData":[TD([[makeQuery(id+"F7.imprint","IMPRINT",EDGE,{"derivedFrom":sQuery(id+"F7.wireOp",EDGE,"E105.MirrorCS")}),1.0]])]});
            extrude(context, id + "F9", {"entities" : qUnion([Q0, Q1, Q2, Q3, Q4, Q5, Q6, Q7, Q8, Q9, Q10, Q11, Q12, Q13, Q14]), "operationType" : NewBodyOperationType.ADD, "depth" : 5 * mm, "offsetDistance" : 25 * mm});
        }
    });
